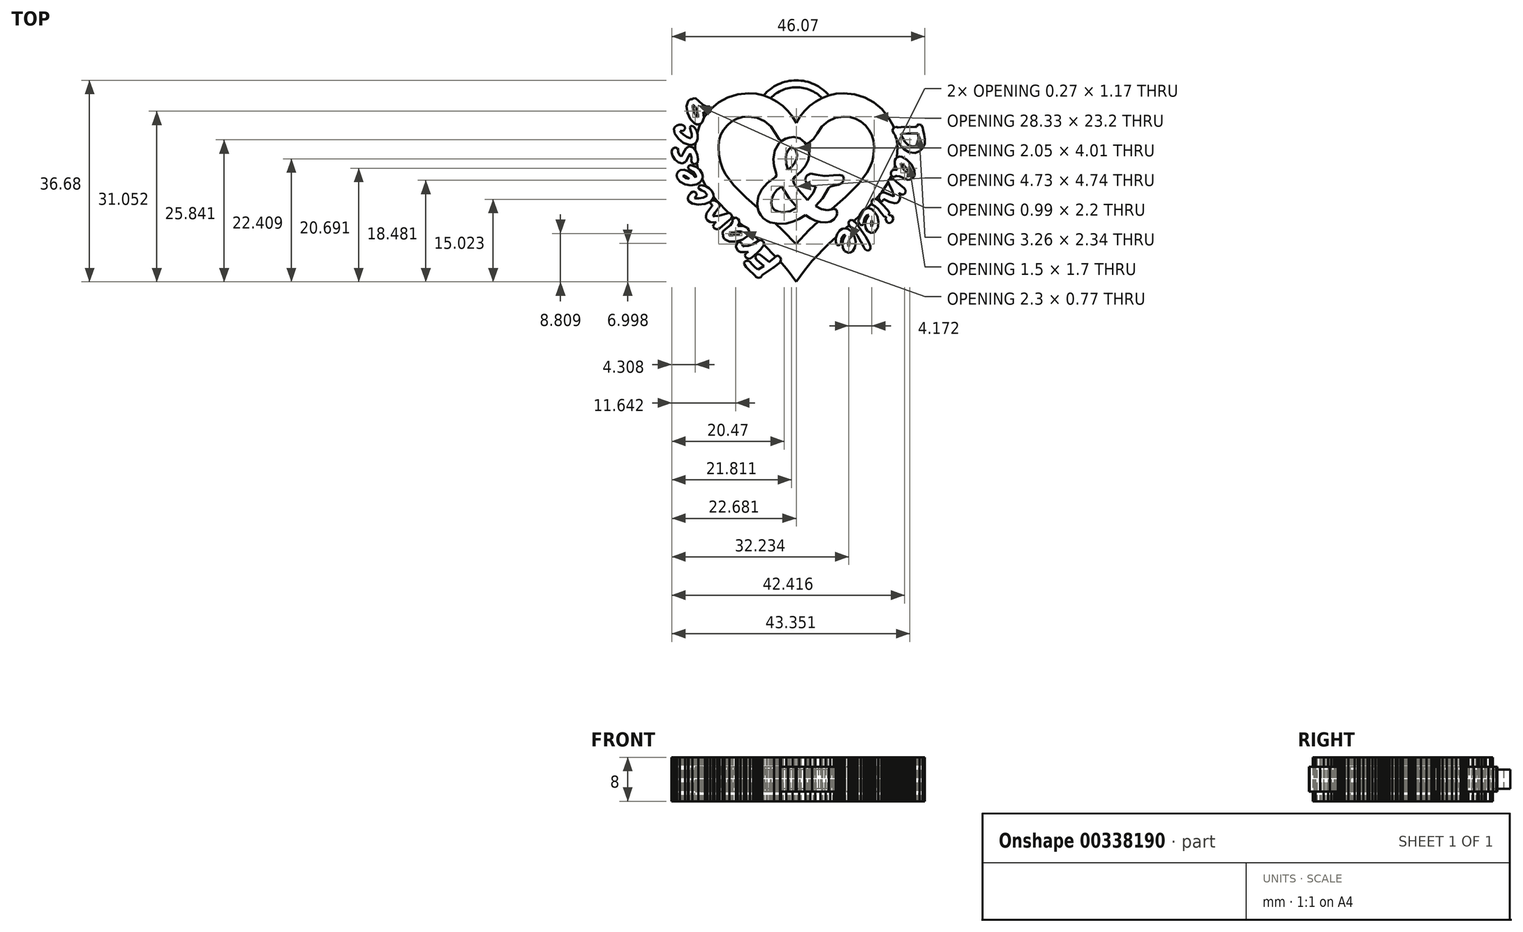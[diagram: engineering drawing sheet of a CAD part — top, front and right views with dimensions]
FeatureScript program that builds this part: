
annotation { "Feature Type Name" : "Feature", "Feature Type Description" : "" }
export const myFeature = defineFeature(function(context is Context, id is Id, definition is map)
    precondition{}
    {
        {
            var Q0;
            Q0=qCreatedBy(makeId("Top.planeOp"),FACE);
            var sketch = newSketch(context, id + "F0", { "sketchPlane" : qUnion([Q0])});
            skLineSegment(sketch, "E0", {"start": v(5.9, -10.24) * mm, "end": v(6.97, -10.8) * mm});
            skLineSegment(sketch, "E1", {"start": v(6.97, -10.8) * mm, "end": v(8.06, -10.99) * mm});
            skLineSegment(sketch, "E2", {"start": v(8.06, -10.99) * mm, "end": v(9.01, -10.77) * mm});
            skLineSegment(sketch, "E3", {"start": v(9.01, -10.77) * mm, "end": v(9.22, -10.74) * mm});
            skLineSegment(sketch, "E4", {"start": v(9.22, -10.74) * mm, "end": v(9.68, -10.95) * mm});
            skLineSegment(sketch, "E5", {"start": v(9.68, -10.95) * mm, "end": v(9.83, -11.55) * mm});
            skLineSegment(sketch, "E6", {"start": v(9.83, -11.55) * mm, "end": v(9.68, -12.04) * mm});
            skLineSegment(sketch, "E7", {"start": v(9.68, -12.04) * mm, "end": v(9.22, -12.62) * mm});
            skLineSegment(sketch, "E8", {"start": v(9.22, -12.62) * mm, "end": v(8.56, -13.08) * mm});
            skLineSegment(sketch, "E9", {"start": v(8.56, -13.08) * mm, "end": v(7.74, -13.23) * mm});
            skLineSegment(sketch, "E10", {"start": v(7.74, -13.23) * mm, "end": v(6.78, -13.15) * mm});
            skLineSegment(sketch, "E11", {"start": v(6.78, -13.15) * mm, "end": v(5.84, -12.9) * mm});
            skLineSegment(sketch, "E12", {"start": v(5.84, -12.9) * mm, "end": v(4.92, -12.48) * mm});
            skLineSegment(sketch, "E13", {"start": v(4.92, -12.48) * mm, "end": v(4.02, -11.89) * mm});
            skLineSegment(sketch, "E14", {"start": v(4.02, -11.89) * mm, "end": v(2.89, -12.59) * mm});
            skLineSegment(sketch, "E15", {"start": v(2.89, -12.59) * mm, "end": v(1.72, -13.09) * mm});
            skLineSegment(sketch, "E16", {"start": v(1.72, -13.09) * mm, "end": v(0.52, -13.39) * mm});
            skLineSegment(sketch, "E17", {"start": v(0.52, -13.39) * mm, "end": v(-0.72, -13.49) * mm});
            skLineSegment(sketch, "E18", {"start": v(-0.72, -13.49) * mm, "end": v(-2.35, -13.23) * mm});
            skLineSegment(sketch, "E19", {"start": v(-2.35, -13.23) * mm, "end": v(-3.03, -12.9) * mm});
            skLineSegment(sketch, "E20", {"start": v(-3.03, -12.9) * mm, "end": v(-3.63, -12.45) * mm});
            skLineSegment(sketch, "E21", {"start": v(-3.63, -12.45) * mm, "end": v(-4.11, -11.89) * mm});
            skLineSegment(sketch, "E22", {"start": v(-4.11, -11.89) * mm, "end": v(-4.46, -11.25) * mm});
            skLineSegment(sketch, "E23", {"start": v(-4.46, -11.25) * mm, "end": v(-4.67, -10.53) * mm});
            skLineSegment(sketch, "E24", {"start": v(-4.67, -10.53) * mm, "end": v(-4.74, -9.73) * mm});
            skLineSegment(sketch, "E25", {"start": v(-4.74, -9.73) * mm, "end": v(-4.53, -8.43) * mm});
            skLineSegment(sketch, "E26", {"start": v(-4.53, -8.43) * mm, "end": v(-3.91, -7.2) * mm});
            skLineSegment(sketch, "E27", {"start": v(-3.91, -7.2) * mm, "end": v(-2.89, -6.06) * mm});
            skLineSegment(sketch, "E28", {"start": v(-2.89, -6.06) * mm, "end": v(-1.45, -4.98) * mm});
            skLineSegment(sketch, "E29", {"start": v(-1.45, -4.98) * mm, "end": v(-1.22, -4.63) * mm});
            skLineSegment(sketch, "E30", {"start": v(-1.22, -4.63) * mm, "end": v(-1.31, -4.25) * mm});
            skLineSegment(sketch, "E31", {"start": v(-1.31, -4.25) * mm, "end": v(-1.68, -2.95) * mm});
            skLineSegment(sketch, "E32", {"start": v(-1.68, -2.95) * mm, "end": v(-1.8, -1.73) * mm});
            skLineSegment(sketch, "E33", {"start": v(-1.8, -1.73) * mm, "end": v(-1.54, -0.13) * mm});
            skLineSegment(sketch, "E34", {"start": v(-1.54, -0.13) * mm, "end": v(-0.77, 1.17) * mm});
            skLineSegment(sketch, "E35", {"start": v(-0.77, 1.17) * mm, "end": v(-0.21, 1.67) * mm});
            skLineSegment(sketch, "E36", {"start": v(-0.21, 1.67) * mm, "end": v(0.41, 2.02) * mm});
            skLineSegment(sketch, "E37", {"start": v(0.41, 2.02) * mm, "end": v(1.1, 2.24) * mm});
            skLineSegment(sketch, "E38", {"start": v(1.1, 2.24) * mm, "end": v(1.87, 2.31) * mm});
            skLineSegment(sketch, "E39", {"start": v(1.87, 2.31) * mm, "end": v(3.04, 2.07) * mm});
            skLineSegment(sketch, "E40", {"start": v(3.04, 2.07) * mm, "end": v(3.94, 1.35) * mm});
            skLineSegment(sketch, "E41", {"start": v(3.94, 1.35) * mm, "end": v(4.52, 0.31) * mm});
            skLineSegment(sketch, "E42", {"start": v(4.52, 0.31) * mm, "end": v(4.71, -0.86) * mm});
            skLineSegment(sketch, "E43", {"start": v(4.71, -0.86) * mm, "end": v(4.55, -1.9) * mm});
            skLineSegment(sketch, "E44", {"start": v(4.55, -1.9) * mm, "end": v(4.05, -2.94) * mm});
            skLineSegment(sketch, "E45", {"start": v(4.05, -2.94) * mm, "end": v(3.23, -3.96) * mm});
            skLineSegment(sketch, "E46", {"start": v(3.23, -3.96) * mm, "end": v(2.07, -4.98) * mm});
            skLineSegment(sketch, "E47", {"start": v(2.07, -4.98) * mm, "end": v(1.75, -5.47) * mm});
            skLineSegment(sketch, "E48", {"start": v(1.75, -5.47) * mm, "end": v(2.02, -6.2) * mm});
            skLineSegment(sketch, "E49", {"start": v(2.02, -6.2) * mm, "end": v(2.82, -7.37) * mm});
            skLineSegment(sketch, "E50", {"start": v(2.82, -7.37) * mm, "end": v(4.42, -9.15) * mm});
            skLineSegment(sketch, "E51", {"start": v(4.42, -9.15) * mm, "end": v(5.4, -7.88) * mm});
            skLineSegment(sketch, "E52", {"start": v(5.4, -7.88) * mm, "end": v(5.96, -6.65) * mm});
            skLineSegment(sketch, "E53", {"start": v(5.96, -6.65) * mm, "end": v(5.59, -6.6) * mm});
            skLineSegment(sketch, "E54", {"start": v(5.59, -6.6) * mm, "end": v(4.82, -6.47) * mm});
            skLineSegment(sketch, "E55", {"start": v(4.82, -6.47) * mm, "end": v(4.35, -6.22) * mm});
            skLineSegment(sketch, "E56", {"start": v(4.35, -6.22) * mm, "end": v(4.12, -5.83) * mm});
            skLineSegment(sketch, "E57", {"start": v(4.12, -5.83) * mm, "end": v(4.04, -5.33) * mm});
            skLineSegment(sketch, "E58", {"start": v(4.04, -5.33) * mm, "end": v(4.12, -4.97) * mm});
            skLineSegment(sketch, "E59", {"start": v(4.12, -4.97) * mm, "end": v(4.36, -4.65) * mm});
            skLineSegment(sketch, "E60", {"start": v(4.36, -4.65) * mm, "end": v(5, -4.34) * mm});
            skLineSegment(sketch, "E61", {"start": v(5, -4.34) * mm, "end": v(5.96, -4.55) * mm});
            skLineSegment(sketch, "E62", {"start": v(5.96, -4.55) * mm, "end": v(7.52, -4.77) * mm});
            skLineSegment(sketch, "E63", {"start": v(7.52, -4.77) * mm, "end": v(9.12, -4.67) * mm});
            skLineSegment(sketch, "E64", {"start": v(9.12, -4.67) * mm, "end": v(10.22, -4.57) * mm});
            skLineSegment(sketch, "E65", {"start": v(10.22, -4.57) * mm, "end": v(10.8, -4.73) * mm});
            skLineSegment(sketch, "E66", {"start": v(10.8, -4.73) * mm, "end": v(11, -5.2) * mm});
            skLineSegment(sketch, "E67", {"start": v(11, -5.2) * mm, "end": v(10.9, -5.72) * mm});
            skLineSegment(sketch, "E68", {"start": v(10.9, -5.72) * mm, "end": v(10.6, -6.11) * mm});
            skLineSegment(sketch, "E69", {"start": v(10.6, -6.11) * mm, "end": v(10.1, -6.37) * mm});
            skLineSegment(sketch, "E70", {"start": v(10.1, -6.37) * mm, "end": v(9.4, -6.5) * mm});
            skLineSegment(sketch, "E71", {"start": v(9.4, -6.5) * mm, "end": v(8.61, -6.65) * mm});
            skLineSegment(sketch, "E72", {"start": v(8.61, -6.65) * mm, "end": v(8.26, -7) * mm});
            skLineSegment(sketch, "E73", {"start": v(8.26, -7) * mm, "end": v(7.13, -8.84) * mm});
            skLineSegment(sketch, "E74", {"start": v(7.13, -8.84) * mm, "end": v(5.9, -10.24) * mm});
            skLineSegment(sketch, "E75", {"start": v(0.89, -3.63) * mm, "end": v(1.6, -2.98) * mm});
            skLineSegment(sketch, "E76", {"start": v(1.6, -2.98) * mm, "end": v(2.12, -2.3) * mm});
            skLineSegment(sketch, "E77", {"start": v(2.12, -2.3) * mm, "end": v(2.42, -1.62) * mm});
            skLineSegment(sketch, "E78", {"start": v(2.42, -1.62) * mm, "end": v(2.53, -0.92) * mm});
            skLineSegment(sketch, "E79", {"start": v(2.53, -0.92) * mm, "end": v(2.26, -0.02) * mm});
            skLineSegment(sketch, "E80", {"start": v(2.26, -0.02) * mm, "end": v(1.99, 0.27) * mm});
            skLineSegment(sketch, "E81", {"start": v(1.99, 0.27) * mm, "end": v(1.65, 0.37) * mm});
            skLineSegment(sketch, "E82", {"start": v(1.65, 0.37) * mm, "end": v(1.21, 0.23) * mm});
            skLineSegment(sketch, "E83", {"start": v(1.21, 0.23) * mm, "end": v(0.83, -0.18) * mm});
            skLineSegment(sketch, "E84", {"start": v(0.83, -0.18) * mm, "end": v(0.56, -0.78) * mm});
            skLineSegment(sketch, "E85", {"start": v(0.56, -0.78) * mm, "end": v(0.48, -1.49) * mm});
            skLineSegment(sketch, "E86", {"start": v(0.48, -1.49) * mm, "end": v(0.58, -2.59) * mm});
            skLineSegment(sketch, "E87", {"start": v(0.58, -2.59) * mm, "end": v(0.89, -3.63) * mm});
            skLineSegment(sketch, "E88", {"start": v(2.53, -10.51) * mm, "end": v(1.02, -8.73) * mm});
            skLineSegment(sketch, "E89", {"start": v(1.02, -8.73) * mm, "end": v(-0.3, -6.65) * mm});
            skLineSegment(sketch, "E90", {"start": v(-0.3, -6.65) * mm, "end": v(-1.14, -7.32) * mm});
            skLineSegment(sketch, "E91", {"start": v(-1.14, -7.32) * mm, "end": v(-1.73, -8.05) * mm});
            skLineSegment(sketch, "E92", {"start": v(-1.73, -8.05) * mm, "end": v(-2.09, -8.82) * mm});
            skLineSegment(sketch, "E93", {"start": v(-2.09, -8.82) * mm, "end": v(-2.2, -9.64) * mm});
            skLineSegment(sketch, "E94", {"start": v(-2.2, -9.64) * mm, "end": v(-2.06, -10.37) * mm});
            skLineSegment(sketch, "E95", {"start": v(-2.06, -10.37) * mm, "end": v(-1.62, -10.93) * mm});
            skLineSegment(sketch, "E96", {"start": v(-1.62, -10.93) * mm, "end": v(-0.93, -11.27) * mm});
            skLineSegment(sketch, "E97", {"start": v(-0.93, -11.27) * mm, "end": v(-0.03, -11.39) * mm});
            skLineSegment(sketch, "E98", {"start": v(-0.03, -11.39) * mm, "end": v(1.25, -11.17) * mm});
            skLineSegment(sketch, "E99", {"start": v(1.25, -11.17) * mm, "end": v(2.53, -10.51) * mm});
            skLineSegment(sketch, "E100", {"start": v(-6.3, 10.29) * mm, "end": v(-8.27, 10.09) * mm});
            skLineSegment(sketch, "E101", {"start": v(-8.27, 10.09) * mm, "end": v(-10.1, 9.52) * mm});
            skLineSegment(sketch, "E102", {"start": v(-10.1, 9.52) * mm, "end": v(-11.75, 8.62) * mm});
            skLineSegment(sketch, "E103", {"start": v(-11.75, 8.62) * mm, "end": v(-13.19, 7.43) * mm});
            skLineSegment(sketch, "E104", {"start": v(-13.19, 7.43) * mm, "end": v(-14.37, 5.98) * mm});
            skLineSegment(sketch, "E105", {"start": v(-14.37, 5.98) * mm, "end": v(-15.27, 4.32) * mm});
            skLineSegment(sketch, "E106", {"start": v(-15.27, 4.32) * mm, "end": v(-15.84, 2.5) * mm});
            skLineSegment(sketch, "E107", {"start": v(-16.04, 0.53) * mm, "end": v(-15.91, -1.43) * mm});
            skLineSegment(sketch, "E108", {"start": v(-15.91, -1.43) * mm, "end": v(-15.55, -3.22) * mm});
            skLineSegment(sketch, "E109", {"start": v(-15.55, -3.22) * mm, "end": v(-14.97, -4.87) * mm});
            skLineSegment(sketch, "E110", {"start": v(-14.97, -4.87) * mm, "end": v(-14.2, -6.4) * mm});
            skLineSegment(sketch, "E111", {"start": v(-14.2, -6.4) * mm, "end": v(-13.27, -7.83) * mm});
            skLineSegment(sketch, "E112", {"start": v(-13.27, -7.83) * mm, "end": v(-12.18, -9.2) * mm});
            skLineSegment(sketch, "E113", {"start": v(-12.18, -9.2) * mm, "end": v(-9.63, -11.78) * mm});
            skLineSegment(sketch, "E114", {"start": v(-9.63, -11.78) * mm, "end": v(-3.7, -17.11) * mm});
            skLineSegment(sketch, "E115", {"start": v(-3.7, -17.11) * mm, "end": v(-0.64, -20.22) * mm});
            skLineSegment(sketch, "E116", {"start": v(-0.64, -20.22) * mm, "end": v(0.84, -21.97) * mm});
            skLineSegment(sketch, "E117", {"start": v(0.84, -21.97) * mm, "end": v(2.26, -23.88) * mm});
            skLineSegment(sketch, "E118", {"start": v(2.26, -23.88) * mm, "end": v(2.37, -24.04) * mm});
            skLineSegment(sketch, "E119", {"start": v(2.37, -24.04) * mm, "end": v(2.48, -23.88) * mm});
            skLineSegment(sketch, "E120", {"start": v(2.48, -23.88) * mm, "end": v(3.84, -21.98) * mm});
            skLineSegment(sketch, "E121", {"start": v(3.84, -21.98) * mm, "end": v(5.27, -20.23) * mm});
            skLineSegment(sketch, "E122", {"start": v(5.27, -20.23) * mm, "end": v(8.27, -17.1) * mm});
            skLineSegment(sketch, "E123", {"start": v(8.27, -17.1) * mm, "end": v(14.23, -11.68) * mm});
            skLineSegment(sketch, "E124", {"start": v(14.23, -11.68) * mm, "end": v(16.81, -9.06) * mm});
            skLineSegment(sketch, "E125", {"start": v(16.81, -9.06) * mm, "end": v(17.93, -7.7) * mm});
            skLineSegment(sketch, "E126", {"start": v(17.93, -7.7) * mm, "end": v(18.89, -6.26) * mm});
            skLineSegment(sketch, "E127", {"start": v(18.89, -6.26) * mm, "end": v(19.68, -4.75) * mm});
            skLineSegment(sketch, "E128", {"start": v(19.68, -4.75) * mm, "end": v(20.28, -3.12) * mm});
            skLineSegment(sketch, "E129", {"start": v(20.28, -3.12) * mm, "end": v(20.65, -1.37) * mm});
            skLineSegment(sketch, "E130", {"start": v(20.65, -1.37) * mm, "end": v(20.78, 0.53) * mm});
            skLineSegment(sketch, "E131", {"start": v(20.78, 0.53) * mm, "end": v(20.58, 2.5) * mm});
            skLineSegment(sketch, "E132", {"start": v(20.58, 2.5) * mm, "end": v(20.01, 4.32) * mm});
            skLineSegment(sketch, "E133", {"start": v(20.01, 4.32) * mm, "end": v(19.12, 5.98) * mm});
            skLineSegment(sketch, "E134", {"start": v(19.12, 5.98) * mm, "end": v(17.93, 7.43) * mm});
            skLineSegment(sketch, "E135", {"start": v(17.93, 7.43) * mm, "end": v(16.49, 8.62) * mm});
            skLineSegment(sketch, "E136", {"start": v(16.49, 8.62) * mm, "end": v(14.84, 9.52) * mm});
            skLineSegment(sketch, "E137", {"start": v(14.84, 9.52) * mm, "end": v(13, 10.09) * mm});
            skLineSegment(sketch, "E138", {"start": v(13, 10.09) * mm, "end": v(11.05, 10.29) * mm});
            skLineSegment(sketch, "E139", {"start": v(11.05, 10.29) * mm, "end": v(9.65, 10.18) * mm});
            skLineSegment(sketch, "E140", {"start": v(9.65, 10.18) * mm, "end": v(8.3, 9.89) * mm});
            skLineSegment(sketch, "E141", {"start": v(8.3, 9.89) * mm, "end": v(7.05, 9.41) * mm});
            skLineSegment(sketch, "E142", {"start": v(7.05, 9.41) * mm, "end": v(5.88, 8.77) * mm});
            skLineSegment(sketch, "E143", {"start": v(5.88, 8.77) * mm, "end": v(4.81, 7.98) * mm});
            skLineSegment(sketch, "E144", {"start": v(4.81, 7.98) * mm, "end": v(3.86, 7.05) * mm});
            skLineSegment(sketch, "E145", {"start": v(3.86, 7.05) * mm, "end": v(3.05, 6) * mm});
            skLineSegment(sketch, "E146", {"start": v(3.05, 6) * mm, "end": v(2.37, 4.85) * mm});
            skLineSegment(sketch, "E147", {"start": v(2.37, 4.85) * mm, "end": v(1.7, 6) * mm});
            skLineSegment(sketch, "E148", {"start": v(1.7, 6) * mm, "end": v(0.88, 7.05) * mm});
            skLineSegment(sketch, "E149", {"start": v(0.88, 7.05) * mm, "end": v(-0.07, 7.98) * mm});
            skLineSegment(sketch, "E150", {"start": v(-0.07, 7.98) * mm, "end": v(-1.14, 8.77) * mm});
            skLineSegment(sketch, "E151", {"start": v(-1.14, 8.77) * mm, "end": v(-2.3, 9.41) * mm});
            skLineSegment(sketch, "E152", {"start": v(-2.3, 9.41) * mm, "end": v(-3.57, 9.89) * mm});
            skLineSegment(sketch, "E153", {"start": v(-3.57, 9.89) * mm, "end": v(-4.9, 10.18) * mm});
            skLineSegment(sketch, "E154", {"start": v(-4.9, 10.18) * mm, "end": v(-6.3, 10.29) * mm});
            skLineSegment(sketch, "E155", {"start": v(-6.3, 6.04) * mm, "end": v(-7.42, 5.93) * mm});
            skLineSegment(sketch, "E156", {"start": v(-7.42, 5.93) * mm, "end": v(-8.46, 5.61) * mm});
            skLineSegment(sketch, "E157", {"start": v(-8.46, 5.61) * mm, "end": v(-9.39, 5.11) * mm});
            skLineSegment(sketch, "E158", {"start": v(-9.39, 5.11) * mm, "end": v(-10.2, 4.44) * mm});
            skLineSegment(sketch, "E159", {"start": v(-10.2, 4.44) * mm, "end": v(-10.86, 3.63) * mm});
            skLineSegment(sketch, "E160", {"start": v(-10.86, 3.63) * mm, "end": v(-11.37, 2.7) * mm});
            skLineSegment(sketch, "E161", {"start": v(-11.37, 2.7) * mm, "end": v(-11.68, 1.65) * mm});
            skLineSegment(sketch, "E162", {"start": v(-11.68, 1.65) * mm, "end": v(-11.8, 0.53) * mm});
            skLineSegment(sketch, "E163", {"start": v(-11.8, 0.53) * mm, "end": v(-11.71, -0.9) * mm});
            skLineSegment(sketch, "E164", {"start": v(-11.71, -0.9) * mm, "end": v(-11.48, -2.17) * mm});
            skLineSegment(sketch, "E165", {"start": v(-11.48, -2.17) * mm, "end": v(-11.09, -3.32) * mm});
            skLineSegment(sketch, "E166", {"start": v(-11.09, -3.32) * mm, "end": v(-10.53, -4.4) * mm});
            skLineSegment(sketch, "E167", {"start": v(-10.53, -4.4) * mm, "end": v(-8.96, -6.48) * mm});
            skLineSegment(sketch, "E168", {"start": v(-8.96, -6.48) * mm, "end": v(-6.74, -8.68) * mm});
            skLineSegment(sketch, "E169", {"start": v(-6.74, -8.68) * mm, "end": v(-2.5, -12.45) * mm});
            skLineSegment(sketch, "E170", {"start": v(-2.5, -12.45) * mm, "end": v(-0.12, -14.65) * mm});
            skLineSegment(sketch, "E171", {"start": v(-0.12, -14.65) * mm, "end": v(2.31, -17.16) * mm});
            skLineSegment(sketch, "E172", {"start": v(2.31, -17.16) * mm, "end": v(4.7, -14.64) * mm});
            skLineSegment(sketch, "E173", {"start": v(4.7, -14.64) * mm, "end": v(7.06, -12.4) * mm});
            skLineSegment(sketch, "E174", {"start": v(7.06, -12.4) * mm, "end": v(11.33, -8.58) * mm});
            skLineSegment(sketch, "E175", {"start": v(11.33, -8.58) * mm, "end": v(13.6, -6.32) * mm});
            skLineSegment(sketch, "E176", {"start": v(13.6, -6.32) * mm, "end": v(15.23, -4.22) * mm});
            skLineSegment(sketch, "E177", {"start": v(15.23, -4.22) * mm, "end": v(15.8, -3.15) * mm});
            skLineSegment(sketch, "E178", {"start": v(15.8, -3.15) * mm, "end": v(16.2, -2.03) * mm});
            skLineSegment(sketch, "E179", {"start": v(16.2, -2.03) * mm, "end": v(16.45, -0.81) * mm});
            skLineSegment(sketch, "E180", {"start": v(16.45, -0.81) * mm, "end": v(16.53, 0.53) * mm});
            skLineSegment(sketch, "E181", {"start": v(16.53, 0.53) * mm, "end": v(16.42, 1.65) * mm});
            skLineSegment(sketch, "E182", {"start": v(16.42, 1.65) * mm, "end": v(16.1, 2.7) * mm});
            skLineSegment(sketch, "E183", {"start": v(16.1, 2.7) * mm, "end": v(15.6, 3.63) * mm});
            skLineSegment(sketch, "E184", {"start": v(15.6, 3.63) * mm, "end": v(14.94, 4.44) * mm});
            skLineSegment(sketch, "E185", {"start": v(14.94, 4.44) * mm, "end": v(14.13, 5.11) * mm});
            skLineSegment(sketch, "E186", {"start": v(14.13, 5.11) * mm, "end": v(13.2, 5.61) * mm});
            skLineSegment(sketch, "E187", {"start": v(13.2, 5.61) * mm, "end": v(12.17, 5.93) * mm});
            skLineSegment(sketch, "E188", {"start": v(12.17, 5.93) * mm, "end": v(11.05, 6.04) * mm});
            skLineSegment(sketch, "E189", {"start": v(11.05, 6.04) * mm, "end": v(9.5, 5.82) * mm});
            skLineSegment(sketch, "E190", {"start": v(9.5, 5.82) * mm, "end": v(8.14, 5.2) * mm});
            skLineSegment(sketch, "E191", {"start": v(8.14, 5.2) * mm, "end": v(7.02, 4.22) * mm});
            skLineSegment(sketch, "E192", {"start": v(7.02, 4.22) * mm, "end": v(6.17, 2.96) * mm});
            skLineSegment(sketch, "E193", {"start": v(6.17, 2.96) * mm, "end": v(5.5, 1.98) * mm});
            skLineSegment(sketch, "E194", {"start": v(5.5, 1.98) * mm, "end": v(4.6, 1.24) * mm});
            skLineSegment(sketch, "E195", {"start": v(4.6, 1.24) * mm, "end": v(3.54, 0.77) * mm});
            skLineSegment(sketch, "E196", {"start": v(3.54, 0.77) * mm, "end": v(2.37, 0.6) * mm});
            skLineSegment(sketch, "E197", {"start": v(2.37, 0.6) * mm, "end": v(1.2, 0.77) * mm});
            skLineSegment(sketch, "E198", {"start": v(1.2, 0.77) * mm, "end": v(0.14, 1.24) * mm});
            skLineSegment(sketch, "E199", {"start": v(0.14, 1.24) * mm, "end": v(-0.76, 1.98) * mm});
            skLineSegment(sketch, "E200", {"start": v(-0.76, 1.98) * mm, "end": v(-1.43, 2.96) * mm});
            skLineSegment(sketch, "E201", {"start": v(-1.43, 2.96) * mm, "end": v(-2.27, 4.22) * mm});
            skLineSegment(sketch, "E202", {"start": v(-2.27, 4.22) * mm, "end": v(-3.4, 5.2) * mm});
            skLineSegment(sketch, "E203", {"start": v(-3.4, 5.2) * mm, "end": v(-4.76, 5.82) * mm});
            skLineSegment(sketch, "E204", {"start": v(-4.76, 5.82) * mm, "end": v(-6.3, 6.04) * mm});
            skLineSegment(sketch, "E205", {"start": v(-1.06, -21.53) * mm, "end": v(-1.06, -21.54) * mm});
            skLineSegment(sketch, "E206", {"start": v(-1.06, -21.54) * mm, "end": v(-1.06, -21.54) * mm});
            skLineSegment(sketch, "E207", {"start": v(-1.06, -21.54) * mm, "end": v(-1.06, -21.53) * mm});
            skLineSegment(sketch, "E208", {"start": v(-16.09, 9.4) * mm, "end": v(-16.4, 9.34) * mm});
            skLineSegment(sketch, "E209", {"start": v(-16.4, 9.34) * mm, "end": v(-16.55, 9.2) * mm});
            skLineSegment(sketch, "E210", {"start": v(-16.55, 9.2) * mm, "end": v(-16.93, 9.2) * mm});
            skLineSegment(sketch, "E211", {"start": v(-16.93, 9.2) * mm, "end": v(-17.32, 8.89) * mm});
            skLineSegment(sketch, "E212", {"start": v(-17.32, 8.89) * mm, "end": v(-17.61, 7.94) * mm});
            skLineSegment(sketch, "E213", {"start": v(-17.61, 7.94) * mm, "end": v(-17.42, 6.73) * mm});
            skLineSegment(sketch, "E214", {"start": v(-17.42, 6.73) * mm, "end": v(-16.9, 5.6) * mm});
            skLineSegment(sketch, "E215", {"start": v(-16.9, 5.6) * mm, "end": v(-16.17, 4.82) * mm});
            skLineSegment(sketch, "E216", {"start": v(-16.17, 4.82) * mm, "end": v(-15.79, 4.64) * mm});
            skLineSegment(sketch, "E217", {"start": v(-15.79, 4.64) * mm, "end": v(-15.38, 4.62) * mm});
            skLineSegment(sketch, "E218", {"start": v(-15.38, 4.62) * mm, "end": v(-15, 4.75) * mm});
            skLineSegment(sketch, "E219", {"start": v(-15, 4.75) * mm, "end": v(-14.73, 5) * mm});
            skLineSegment(sketch, "E220", {"start": v(-14.73, 5) * mm, "end": v(-14.47, 5.81) * mm});
            skLineSegment(sketch, "E221", {"start": v(-14.47, 5.81) * mm, "end": v(-14.57, 6.84) * mm});
            skLineSegment(sketch, "E222", {"start": v(-14.57, 6.84) * mm, "end": v(-14.04, 6.63) * mm});
            skLineSegment(sketch, "E223", {"start": v(-14.04, 6.63) * mm, "end": v(-13.62, 6.67) * mm});
            skLineSegment(sketch, "E224", {"start": v(-13.62, 6.67) * mm, "end": v(-13.3, 6.92) * mm});
            skLineSegment(sketch, "E225", {"start": v(-13.3, 6.92) * mm, "end": v(-13.15, 7.4) * mm});
            skLineSegment(sketch, "E226", {"start": v(-13.15, 7.4) * mm, "end": v(-13.15, 7.4) * mm});
            skLineSegment(sketch, "E227", {"start": v(-13.15, 7.4) * mm, "end": v(-13.38, 7.9) * mm});
            skLineSegment(sketch, "E228", {"start": v(-13.38, 7.9) * mm, "end": v(-13.82, 7.89) * mm});
            skLineSegment(sketch, "E229", {"start": v(-13.82, 7.89) * mm, "end": v(-13.82, 7.89) * mm});
            skLineSegment(sketch, "E230", {"start": v(-13.82, 7.89) * mm, "end": v(-13.89, 7.84) * mm});
            skLineSegment(sketch, "E231", {"start": v(-13.89, 7.84) * mm, "end": v(-14.1, 7.9) * mm});
            skLineSegment(sketch, "E232", {"start": v(-14.1, 7.9) * mm, "end": v(-14.61, 8.18) * mm});
            skLineSegment(sketch, "E233", {"start": v(-14.61, 8.18) * mm, "end": v(-15.46, 8.93) * mm});
            skLineSegment(sketch, "E234", {"start": v(-15.46, 8.93) * mm, "end": v(-15.46, 8.93) * mm});
            skLineSegment(sketch, "E235", {"start": v(-15.46, 8.93) * mm, "end": v(-15.89, 9.32) * mm});
            skLineSegment(sketch, "E236", {"start": v(-15.89, 9.32) * mm, "end": v(-16.09, 9.4) * mm});
            skLineSegment(sketch, "E237", {"start": v(-16.09, 9.4) * mm, "end": v(-16.09, 9.4) * mm});
            skLineSegment(sketch, "E238", {"start": v(-16.42, 8.11) * mm, "end": v(-16.27, 8.05) * mm});
            skLineSegment(sketch, "E239", {"start": v(-16.27, 8.05) * mm, "end": v(-15.92, 7.65) * mm});
            skLineSegment(sketch, "E240", {"start": v(-15.92, 7.65) * mm, "end": v(-15.63, 6.93) * mm});
            skLineSegment(sketch, "E241", {"start": v(-15.63, 6.93) * mm, "end": v(-15.5, 6.3) * mm});
            skLineSegment(sketch, "E242", {"start": v(-15.5, 6.3) * mm, "end": v(-15.54, 5.91) * mm});
            skLineSegment(sketch, "E243", {"start": v(-15.54, 5.91) * mm, "end": v(-15.6, 5.95) * mm});
            skLineSegment(sketch, "E244", {"start": v(-15.6, 5.95) * mm, "end": v(-15.97, 6.35) * mm});
            skLineSegment(sketch, "E245", {"start": v(-15.97, 6.35) * mm, "end": v(-16.31, 7.08) * mm});
            skLineSegment(sketch, "E246", {"start": v(-16.31, 7.08) * mm, "end": v(-16.31, 7.08) * mm});
            skLineSegment(sketch, "E247", {"start": v(-16.31, 7.08) * mm, "end": v(-16.5, 7.8) * mm});
            skLineSegment(sketch, "E248", {"start": v(-16.5, 7.8) * mm, "end": v(-16.46, 8.1) * mm});
            skLineSegment(sketch, "E249", {"start": v(-16.46, 8.1) * mm, "end": v(-16.43, 8.1) * mm});
            skLineSegment(sketch, "E250", {"start": v(-16.43, 8.1) * mm, "end": v(-16.42, 8.11) * mm});
            skLineSegment(sketch, "E251", {"start": v(-16.42, 8.11) * mm, "end": v(-16.42, 8.11) * mm});
            skLineSegment(sketch, "E252", {"start": v(24.67, 4.62) * mm, "end": v(24.36, 4.42) * mm});
            skLineSegment(sketch, "E253", {"start": v(24.36, 4.42) * mm, "end": v(24.28, 4.15) * mm});
            skLineSegment(sketch, "E254", {"start": v(24.28, 4.15) * mm, "end": v(23.96, 4.15) * mm});
            skLineSegment(sketch, "E255", {"start": v(23.96, 4.15) * mm, "end": v(23.96, 4.15) * mm});
            skLineSegment(sketch, "E256", {"start": v(23.96, 4.15) * mm, "end": v(21.45, 4.1) * mm});
            skLineSegment(sketch, "E257", {"start": v(21.45, 4.1) * mm, "end": v(21.45, 4.1) * mm});
            skLineSegment(sketch, "E258", {"start": v(21.45, 4.1) * mm, "end": v(20.9, 4.08) * mm});
            skLineSegment(sketch, "E259", {"start": v(20.9, 4.08) * mm, "end": v(20.7, 4.13) * mm});
            skLineSegment(sketch, "E260", {"start": v(20.7, 4.13) * mm, "end": v(20.72, 4.12) * mm});
            skLineSegment(sketch, "E261", {"start": v(20.72, 4.12) * mm, "end": v(20.42, 4.17) * mm});
            skLineSegment(sketch, "E262", {"start": v(20.42, 4.17) * mm, "end": v(20.05, 3.94) * mm});
            skLineSegment(sketch, "E263", {"start": v(20.05, 3.94) * mm, "end": v(19.87, 3.45) * mm});
            skLineSegment(sketch, "E264", {"start": v(19.87, 3.45) * mm, "end": v(20.14, 2.92) * mm});
            skLineSegment(sketch, "E265", {"start": v(20.14, 2.92) * mm, "end": v(20.14, 2.92) * mm});
            skLineSegment(sketch, "E266", {"start": v(20.14, 2.92) * mm, "end": v(20.33, 2.65) * mm});
            skLineSegment(sketch, "E267", {"start": v(20.33, 2.65) * mm, "end": v(20.51, 2.23) * mm});
            skLineSegment(sketch, "E268", {"start": v(20.51, 2.23) * mm, "end": v(20.51, 2.23) * mm});
            skLineSegment(sketch, "E269", {"start": v(20.51, 2.23) * mm, "end": v(21.1, 1.06) * mm});
            skLineSegment(sketch, "E270", {"start": v(21.1, 1.06) * mm, "end": v(21.93, 0.13) * mm});
            skLineSegment(sketch, "E271", {"start": v(21.93, 0.13) * mm, "end": v(21.93, 0.13) * mm});
            skLineSegment(sketch, "E272", {"start": v(21.93, 0.13) * mm, "end": v(22.92, -0.46) * mm});
            skLineSegment(sketch, "E273", {"start": v(22.92, -0.46) * mm, "end": v(23.96, -0.57) * mm});
            skLineSegment(sketch, "E274", {"start": v(23.96, -0.57) * mm, "end": v(24.8, -0.3) * mm});
            skLineSegment(sketch, "E275", {"start": v(24.8, -0.3) * mm, "end": v(25.4, 0.29) * mm});
            skLineSegment(sketch, "E276", {"start": v(25.4, 0.29) * mm, "end": v(25.74, 1.08) * mm});
            skLineSegment(sketch, "E277", {"start": v(25.74, 1.08) * mm, "end": v(25.76, 2) * mm});
            skLineSegment(sketch, "E278", {"start": v(25.76, 2) * mm, "end": v(25.61, 2.77) * mm});
            skLineSegment(sketch, "E279", {"start": v(25.61, 2.77) * mm, "end": v(25.61, 2.77) * mm});
            skLineSegment(sketch, "E280", {"start": v(25.61, 2.77) * mm, "end": v(25.45, 3.6) * mm});
            skLineSegment(sketch, "E281", {"start": v(25.45, 3.6) * mm, "end": v(25.4, 4.05) * mm});
            skLineSegment(sketch, "E282", {"start": v(25.4, 4.05) * mm, "end": v(25.4, 4.05) * mm});
            skLineSegment(sketch, "E283", {"start": v(25.4, 4.05) * mm, "end": v(25.14, 4.47) * mm});
            skLineSegment(sketch, "E284", {"start": v(25.14, 4.47) * mm, "end": v(24.67, 4.62) * mm});
            skLineSegment(sketch, "E285", {"start": v(24.67, 4.62) * mm, "end": v(24.67, 4.62) * mm});
            skLineSegment(sketch, "E286", {"start": v(-18.93, 4.57) * mm, "end": v(-19.35, 4.44) * mm});
            skLineSegment(sketch, "E287", {"start": v(-19.35, 4.44) * mm, "end": v(-19.7, 4.17) * mm});
            skLineSegment(sketch, "E288", {"start": v(-19.7, 4.17) * mm, "end": v(-19.9, 3.8) * mm});
            skLineSegment(sketch, "E289", {"start": v(-19.9, 3.8) * mm, "end": v(-19.76, 2.94) * mm});
            skLineSegment(sketch, "E290", {"start": v(-19.76, 2.94) * mm, "end": v(-19.09, 2.04) * mm});
            skLineSegment(sketch, "E291", {"start": v(-19.09, 2.04) * mm, "end": v(-18.17, 1.3) * mm});
            skLineSegment(sketch, "E292", {"start": v(-18.17, 1.3) * mm, "end": v(-17.23, 0.92) * mm});
            skLineSegment(sketch, "E293", {"start": v(-17.23, 0.92) * mm, "end": v(-16.65, 0.9) * mm});
            skLineSegment(sketch, "E294", {"start": v(-16.65, 0.9) * mm, "end": v(-16.16, 1.08) * mm});
            skLineSegment(sketch, "E295", {"start": v(-16.16, 1.08) * mm, "end": v(-15.8, 1.47) * mm});
            skLineSegment(sketch, "E296", {"start": v(-15.8, 1.47) * mm, "end": v(-15.6, 2.02) * mm});
            skLineSegment(sketch, "E297", {"start": v(-15.6, 2.02) * mm, "end": v(-15.58, 2.76) * mm});
            skLineSegment(sketch, "E298", {"start": v(-15.58, 2.76) * mm, "end": v(-15.8, 3.5) * mm});
            skLineSegment(sketch, "E299", {"start": v(-15.8, 3.5) * mm, "end": v(-15.8, 3.5) * mm});
            skLineSegment(sketch, "E300", {"start": v(-15.8, 3.5) * mm, "end": v(-16.13, 4.08) * mm});
            skLineSegment(sketch, "E301", {"start": v(-16.13, 4.08) * mm, "end": v(-16.52, 4.36) * mm});
            skLineSegment(sketch, "E302", {"start": v(-16.52, 4.36) * mm, "end": v(-16.82, 4.3) * mm});
            skLineSegment(sketch, "E303", {"start": v(-16.82, 4.3) * mm, "end": v(-16.98, 4.05) * mm});
            skLineSegment(sketch, "E304", {"start": v(-16.98, 4.05) * mm, "end": v(-16.85, 3.47) * mm});
            skLineSegment(sketch, "E305", {"start": v(-16.85, 3.47) * mm, "end": v(-16.86, 3.47) * mm});
            skLineSegment(sketch, "E306", {"start": v(-16.86, 3.47) * mm, "end": v(-16.68, 2.9) * mm});
            skLineSegment(sketch, "E307", {"start": v(-16.68, 2.9) * mm, "end": v(-16.68, 2.39) * mm});
            skLineSegment(sketch, "E308", {"start": v(-16.68, 2.39) * mm, "end": v(-16.8, 2.15) * mm});
            skLineSegment(sketch, "E309", {"start": v(-16.8, 2.15) * mm, "end": v(-17.02, 2.13) * mm});
            skLineSegment(sketch, "E310", {"start": v(-17.02, 2.13) * mm, "end": v(-17.57, 2.33) * mm});
            skLineSegment(sketch, "E311", {"start": v(-17.57, 2.33) * mm, "end": v(-18.2, 2.78) * mm});
            skLineSegment(sketch, "E312", {"start": v(-18.2, 2.78) * mm, "end": v(-18.66, 3.25) * mm});
            skLineSegment(sketch, "E313", {"start": v(-18.66, 3.25) * mm, "end": v(-18.73, 3.4) * mm});
            skLineSegment(sketch, "E314", {"start": v(-18.73, 3.4) * mm, "end": v(-18.6, 3.4) * mm});
            skLineSegment(sketch, "E315", {"start": v(-18.6, 3.4) * mm, "end": v(-18.12, 3.48) * mm});
            skLineSegment(sketch, "E316", {"start": v(-18.12, 3.48) * mm, "end": v(-17.85, 3.86) * mm});
            skLineSegment(sketch, "E317", {"start": v(-17.85, 3.86) * mm, "end": v(-17.95, 4.26) * mm});
            skLineSegment(sketch, "E318", {"start": v(-17.95, 4.26) * mm, "end": v(-17.95, 4.26) * mm});
            skLineSegment(sketch, "E319", {"start": v(-17.95, 4.26) * mm, "end": v(-18.18, 4.46) * mm});
            skLineSegment(sketch, "E320", {"start": v(-18.18, 4.46) * mm, "end": v(-18.5, 4.56) * mm});
            skLineSegment(sketch, "E321", {"start": v(-18.5, 4.56) * mm, "end": v(-18.93, 4.57) * mm});
            skLineSegment(sketch, "E322", {"start": v(-18.93, 4.57) * mm, "end": v(-18.93, 4.57) * mm});
            skLineSegment(sketch, "E323", {"start": v(22.67, 2.97) * mm, "end": v(24.46, 2.96) * mm});
            skLineSegment(sketch, "E324", {"start": v(24.46, 2.96) * mm, "end": v(24.67, 1.98) * mm});
            skLineSegment(sketch, "E325", {"start": v(24.67, 1.98) * mm, "end": v(24.67, 1.46) * mm});
            skLineSegment(sketch, "E326", {"start": v(24.67, 1.46) * mm, "end": v(24.51, 1.05) * mm});
            skLineSegment(sketch, "E327", {"start": v(24.51, 1.05) * mm, "end": v(24.51, 1.05) * mm});
            skLineSegment(sketch, "E328", {"start": v(24.51, 1.05) * mm, "end": v(24.23, 0.77) * mm});
            skLineSegment(sketch, "E329", {"start": v(24.23, 0.77) * mm, "end": v(23.82, 0.63) * mm});
            skLineSegment(sketch, "E330", {"start": v(23.82, 0.63) * mm, "end": v(23.23, 0.67) * mm});
            skLineSegment(sketch, "E331", {"start": v(23.23, 0.67) * mm, "end": v(22.66, 0.95) * mm});
            skLineSegment(sketch, "E332", {"start": v(22.66, 0.95) * mm, "end": v(22.15, 1.45) * mm});
            skLineSegment(sketch, "E333", {"start": v(22.15, 1.45) * mm, "end": v(21.73, 2.13) * mm});
            skLineSegment(sketch, "E334", {"start": v(21.73, 2.13) * mm, "end": v(21.73, 2.13) * mm});
            skLineSegment(sketch, "E335", {"start": v(21.73, 2.13) * mm, "end": v(21.45, 2.77) * mm});
            skLineSegment(sketch, "E336", {"start": v(21.45, 2.77) * mm, "end": v(21.41, 2.89) * mm});
            skLineSegment(sketch, "E337", {"start": v(21.41, 2.89) * mm, "end": v(21.42, 2.9) * mm});
            skLineSegment(sketch, "E338", {"start": v(21.42, 2.9) * mm, "end": v(22.67, 2.97) * mm});
            skLineSegment(sketch, "E339", {"start": v(22.67, 2.97) * mm, "end": v(22.67, 2.97) * mm});
            skLineSegment(sketch, "E340", {"start": v(-17.08, 0.6) * mm, "end": v(-17.7, 0.32) * mm});
            skLineSegment(sketch, "E341", {"start": v(-17.7, 0.32) * mm, "end": v(-18.2, -0.6) * mm});
            skLineSegment(sketch, "E342", {"start": v(-18.2, -0.6) * mm, "end": v(-18.2, -0.6) * mm});
            skLineSegment(sketch, "E343", {"start": v(-18.2, -0.6) * mm, "end": v(-18.45, -1.11) * mm});
            skLineSegment(sketch, "E344", {"start": v(-18.45, -1.11) * mm, "end": v(-18.57, -1.2) * mm});
            skLineSegment(sketch, "E345", {"start": v(-18.57, -1.2) * mm, "end": v(-18.91, -0.94) * mm});
            skLineSegment(sketch, "E346", {"start": v(-18.91, -0.94) * mm, "end": v(-19.14, -0.37) * mm});
            skLineSegment(sketch, "E347", {"start": v(-19.14, -0.37) * mm, "end": v(-19.12, -0.3) * mm});
            skLineSegment(sketch, "E348", {"start": v(-19.12, -0.3) * mm, "end": v(-19.07, -0.07) * mm});
            skLineSegment(sketch, "E349", {"start": v(-19.07, -0.07) * mm, "end": v(-19.25, 0.27) * mm});
            skLineSegment(sketch, "E350", {"start": v(-19.25, 0.27) * mm, "end": v(-19.66, 0.45) * mm});
            skLineSegment(sketch, "E351", {"start": v(-19.66, 0.45) * mm, "end": v(-20.18, 0.2) * mm});
            skLineSegment(sketch, "E352", {"start": v(-20.18, 0.2) * mm, "end": v(-20.31, -0.4) * mm});
            skLineSegment(sketch, "E353", {"start": v(-20.31, -0.4) * mm, "end": v(-20.13, -1.08) * mm});
            skLineSegment(sketch, "E354", {"start": v(-20.13, -1.08) * mm, "end": v(-19.7, -1.77) * mm});
            skLineSegment(sketch, "E355", {"start": v(-19.7, -1.77) * mm, "end": v(-19.1, -2.3) * mm});
            skLineSegment(sketch, "E356", {"start": v(-19.1, -2.3) * mm, "end": v(-18.4, -2.46) * mm});
            skLineSegment(sketch, "E357", {"start": v(-18.4, -2.46) * mm, "end": v(-17.74, -2.16) * mm});
            skLineSegment(sketch, "E358", {"start": v(-17.74, -2.16) * mm, "end": v(-17.74, -2.16) * mm});
            skLineSegment(sketch, "E359", {"start": v(-17.74, -2.16) * mm, "end": v(-17.17, -1.12) * mm});
            skLineSegment(sketch, "E360", {"start": v(-17.17, -1.12) * mm, "end": v(-17.17, -1.12) * mm});
            skLineSegment(sketch, "E361", {"start": v(-17.17, -1.12) * mm, "end": v(-16.97, -0.69) * mm});
            skLineSegment(sketch, "E362", {"start": v(-16.97, -0.69) * mm, "end": v(-16.95, -0.67) * mm});
            skLineSegment(sketch, "E363", {"start": v(-16.95, -0.67) * mm, "end": v(-16.82, -0.93) * mm});
            skLineSegment(sketch, "E364", {"start": v(-16.82, -0.93) * mm, "end": v(-16.67, -1.56) * mm});
            skLineSegment(sketch, "E365", {"start": v(-16.67, -1.56) * mm, "end": v(-16.7, -1.76) * mm});
            skLineSegment(sketch, "E366", {"start": v(-16.7, -1.76) * mm, "end": v(-16.7, -1.76) * mm});
            skLineSegment(sketch, "E367", {"start": v(-16.7, -1.76) * mm, "end": v(-16.74, -2.04) * mm});
            skLineSegment(sketch, "E368", {"start": v(-16.74, -2.04) * mm, "end": v(-16.53, -2.46) * mm});
            skLineSegment(sketch, "E369", {"start": v(-16.53, -2.46) * mm, "end": v(-16.09, -2.62) * mm});
            skLineSegment(sketch, "E370", {"start": v(-16.09, -2.62) * mm, "end": v(-15.6, -2.34) * mm});
            skLineSegment(sketch, "E371", {"start": v(-15.6, -2.34) * mm, "end": v(-15.5, -1.74) * mm});
            skLineSegment(sketch, "E372", {"start": v(-15.5, -1.74) * mm, "end": v(-15.65, -0.88) * mm});
            skLineSegment(sketch, "E373", {"start": v(-15.65, -0.88) * mm, "end": v(-15.98, -0.12) * mm});
            skLineSegment(sketch, "E374", {"start": v(-15.98, -0.12) * mm, "end": v(-15.98, -0.12) * mm});
            skLineSegment(sketch, "E375", {"start": v(-15.98, -0.12) * mm, "end": v(-16.48, 0.43) * mm});
            skLineSegment(sketch, "E376", {"start": v(-16.48, 0.43) * mm, "end": v(-17.08, 0.6) * mm});
            skLineSegment(sketch, "E377", {"start": v(-17.08, 0.6) * mm, "end": v(-17.08, 0.6) * mm});
            skLineSegment(sketch, "E378", {"start": v(21.16, -1.24) * mm, "end": v(20.78, -1.35) * mm});
            skLineSegment(sketch, "E379", {"start": v(20.78, -1.35) * mm, "end": v(20.48, -1.59) * mm});
            skLineSegment(sketch, "E380", {"start": v(20.48, -1.59) * mm, "end": v(20.3, -1.92) * mm});
            skLineSegment(sketch, "E381", {"start": v(20.3, -1.92) * mm, "end": v(20.32, -2.73) * mm});
            skLineSegment(sketch, "E382", {"start": v(20.32, -2.73) * mm, "end": v(20.73, -3.63) * mm});
            skLineSegment(sketch, "E383", {"start": v(20.73, -3.63) * mm, "end": v(20.2, -3.6) * mm});
            skLineSegment(sketch, "E384", {"start": v(20.2, -3.6) * mm, "end": v(19.82, -3.77) * mm});
            skLineSegment(sketch, "E385", {"start": v(19.82, -3.77) * mm, "end": v(19.6, -4.1) * mm});
            skLineSegment(sketch, "E386", {"start": v(19.6, -4.1) * mm, "end": v(19.62, -4.6) * mm});
            skLineSegment(sketch, "E387", {"start": v(19.62, -4.6) * mm, "end": v(19.99, -4.97) * mm});
            skLineSegment(sketch, "E388", {"start": v(19.99, -4.97) * mm, "end": v(20.4, -4.83) * mm});
            skLineSegment(sketch, "E389", {"start": v(20.4, -4.83) * mm, "end": v(20.4, -4.83) * mm});
            skLineSegment(sketch, "E390", {"start": v(20.4, -4.83) * mm, "end": v(20.44, -4.77) * mm});
            skLineSegment(sketch, "E391", {"start": v(20.44, -4.77) * mm, "end": v(20.66, -4.75) * mm});
            skLineSegment(sketch, "E392", {"start": v(20.66, -4.75) * mm, "end": v(20.66, -4.75) * mm});
            skLineSegment(sketch, "E393", {"start": v(20.66, -4.75) * mm, "end": v(21.2, -4.85) * mm});
            skLineSegment(sketch, "E394", {"start": v(21.2, -4.85) * mm, "end": v(22.2, -5.26) * mm});
            skLineSegment(sketch, "E395", {"start": v(22.2, -5.26) * mm, "end": v(22.72, -5.48) * mm});
            skLineSegment(sketch, "E396", {"start": v(22.72, -5.48) * mm, "end": v(23.13, -5.41) * mm});
            skLineSegment(sketch, "E397", {"start": v(23.13, -5.41) * mm, "end": v(23.3, -5.17) * mm});
            skLineSegment(sketch, "E398", {"start": v(23.3, -5.17) * mm, "end": v(23.63, -5.04) * mm});
            skLineSegment(sketch, "E399", {"start": v(23.63, -5.04) * mm, "end": v(23.9, -4.63) * mm});
            skLineSegment(sketch, "E400", {"start": v(23.9, -4.63) * mm, "end": v(23.86, -3.68) * mm});
            skLineSegment(sketch, "E401", {"start": v(23.86, -3.68) * mm, "end": v(23.3, -2.64) * mm});
            skLineSegment(sketch, "E402", {"start": v(23.3, -2.64) * mm, "end": v(23.3, -2.64) * mm});
            skLineSegment(sketch, "E403", {"start": v(23.3, -2.64) * mm, "end": v(22.48, -1.76) * mm});
            skLineSegment(sketch, "E404", {"start": v(22.48, -1.76) * mm, "end": v(21.57, -1.29) * mm});
            skLineSegment(sketch, "E405", {"start": v(21.57, -1.29) * mm, "end": v(21.16, -1.24) * mm});
            skLineSegment(sketch, "E406", {"start": v(21.36, -2.5) * mm, "end": v(21.4, -2.5) * mm});
            skLineSegment(sketch, "E407", {"start": v(21.4, -2.5) * mm, "end": v(21.86, -2.76) * mm});
            skLineSegment(sketch, "E408", {"start": v(21.86, -2.76) * mm, "end": v(22.4, -3.3) * mm});
            skLineSegment(sketch, "E409", {"start": v(22.4, -3.3) * mm, "end": v(22.4, -3.3) * mm});
            skLineSegment(sketch, "E410", {"start": v(22.4, -3.3) * mm, "end": v(22.79, -3.9) * mm});
            skLineSegment(sketch, "E411", {"start": v(22.79, -3.9) * mm, "end": v(22.85, -4.2) * mm});
            skLineSegment(sketch, "E412", {"start": v(22.85, -4.2) * mm, "end": v(22.83, -4.2) * mm});
            skLineSegment(sketch, "E413", {"start": v(22.83, -4.2) * mm, "end": v(22.82, -4.2) * mm});
            skLineSegment(sketch, "E414", {"start": v(22.82, -4.2) * mm, "end": v(22.67, -4.2) * mm});
            skLineSegment(sketch, "E415", {"start": v(22.67, -4.2) * mm, "end": v(22.23, -3.94) * mm});
            skLineSegment(sketch, "E416", {"start": v(22.23, -3.94) * mm, "end": v(21.74, -3.38) * mm});
            skLineSegment(sketch, "E417", {"start": v(21.74, -3.38) * mm, "end": v(21.44, -2.84) * mm});
            skLineSegment(sketch, "E418", {"start": v(21.44, -2.84) * mm, "end": v(21.36, -2.5) * mm});
            skLineSegment(sketch, "E419", {"start": v(-16.77, -2.79) * mm, "end": v(-17.03, -2.83) * mm});
            skLineSegment(sketch, "E420", {"start": v(-17.03, -2.83) * mm, "end": v(-17.28, -3.04) * mm});
            skLineSegment(sketch, "E421", {"start": v(-17.28, -3.04) * mm, "end": v(-17.3, -3.37) * mm});
            skLineSegment(sketch, "E422", {"start": v(-17.3, -3.37) * mm, "end": v(-16.96, -3.67) * mm});
            skLineSegment(sketch, "E423", {"start": v(-16.96, -3.67) * mm, "end": v(-16.25, -4.1) * mm});
            skLineSegment(sketch, "E424", {"start": v(-16.25, -4.1) * mm, "end": v(-15.88, -4.62) * mm});
            skLineSegment(sketch, "E425", {"start": v(-15.88, -4.62) * mm, "end": v(-15.88, -4.9) * mm});
            skLineSegment(sketch, "E426", {"start": v(-15.88, -4.9) * mm, "end": v(-15.98, -5.01) * mm});
            skLineSegment(sketch, "E427", {"start": v(-15.98, -5.01) * mm, "end": v(-16.57, -4.33) * mm});
            skLineSegment(sketch, "E428", {"start": v(-16.57, -4.33) * mm, "end": v(-17.27, -3.86) * mm});
            skLineSegment(sketch, "E429", {"start": v(-17.27, -3.86) * mm, "end": v(-17.27, -3.86) * mm});
            skLineSegment(sketch, "E430", {"start": v(-17.27, -3.86) * mm, "end": v(-18.03, -3.64) * mm});
            skLineSegment(sketch, "E431", {"start": v(-18.03, -3.64) * mm, "end": v(-18.73, -3.72) * mm});
            skLineSegment(sketch, "E432", {"start": v(-18.73, -3.72) * mm, "end": v(-19.07, -3.93) * mm});
            skLineSegment(sketch, "E433", {"start": v(-19.07, -3.93) * mm, "end": v(-19.3, -4.26) * mm});
            skLineSegment(sketch, "E434", {"start": v(-19.3, -4.26) * mm, "end": v(-19.4, -4.67) * mm});
            skLineSegment(sketch, "E435", {"start": v(-19.4, -4.67) * mm, "end": v(-19.32, -5.1) * mm});
            skLineSegment(sketch, "E436", {"start": v(-19.32, -5.1) * mm, "end": v(-18.79, -5.82) * mm});
            skLineSegment(sketch, "E437", {"start": v(-18.79, -5.82) * mm, "end": v(-17.86, -6.3) * mm});
            skLineSegment(sketch, "E438", {"start": v(-17.86, -6.3) * mm, "end": v(-16.78, -6.48) * mm});
            skLineSegment(sketch, "E439", {"start": v(-16.78, -6.48) * mm, "end": v(-15.75, -6.29) * mm});
            skLineSegment(sketch, "E440", {"start": v(-15.75, -6.29) * mm, "end": v(-15.17, -5.96) * mm});
            skLineSegment(sketch, "E441", {"start": v(-15.17, -5.96) * mm, "end": v(-14.8, -5.5) * mm});
            skLineSegment(sketch, "E442", {"start": v(-14.8, -5.5) * mm, "end": v(-14.79, -5.5) * mm});
            skLineSegment(sketch, "E443", {"start": v(-14.79, -5.5) * mm, "end": v(-14.65, -4.94) * mm});
            skLineSegment(sketch, "E444", {"start": v(-14.65, -4.94) * mm, "end": v(-14.77, -4.33) * mm});
            skLineSegment(sketch, "E445", {"start": v(-14.77, -4.33) * mm, "end": v(-15.18, -3.63) * mm});
            skLineSegment(sketch, "E446", {"start": v(-15.18, -3.63) * mm, "end": v(-15.82, -3.1) * mm});
            skLineSegment(sketch, "E447", {"start": v(-15.82, -3.1) * mm, "end": v(-15.83, -3.1) * mm});
            skLineSegment(sketch, "E448", {"start": v(-15.83, -3.1) * mm, "end": v(-16.77, -2.79) * mm});
            skLineSegment(sketch, "E449", {"start": v(-16.77, -2.79) * mm, "end": v(-16.77, -2.79) * mm});
            skLineSegment(sketch, "E450", {"start": v(-17.97, -4.72) * mm, "end": v(-17.6, -4.88) * mm});
            skLineSegment(sketch, "E451", {"start": v(-17.6, -4.88) * mm, "end": v(-17.59, -4.88) * mm});
            skLineSegment(sketch, "E452", {"start": v(-17.59, -4.88) * mm, "end": v(-17.11, -5.26) * mm});
            skLineSegment(sketch, "E453", {"start": v(-17.11, -5.26) * mm, "end": v(-17.71, -5.15) * mm});
            skLineSegment(sketch, "E454", {"start": v(-17.71, -5.15) * mm, "end": v(-18.25, -4.79) * mm});
            skLineSegment(sketch, "E455", {"start": v(-18.25, -4.79) * mm, "end": v(-18.25, -4.77) * mm});
            skLineSegment(sketch, "E456", {"start": v(-18.25, -4.77) * mm, "end": v(-18.25, -4.77) * mm});
            skLineSegment(sketch, "E457", {"start": v(-18.25, -4.77) * mm, "end": v(-18.2, -4.72) * mm});
            skLineSegment(sketch, "E458", {"start": v(-18.2, -4.72) * mm, "end": v(-17.97, -4.72) * mm});
            skLineSegment(sketch, "E459", {"start": v(-17.97, -4.72) * mm, "end": v(-17.97, -4.72) * mm});
            skLineSegment(sketch, "E460", {"start": v(-15.94, -5.07) * mm, "end": v(-15.94, -5.07) * mm});
            skLineSegment(sketch, "E461", {"start": v(19.55, -5.2) * mm, "end": v(19.12, -5.54) * mm});
            skLineSegment(sketch, "E462", {"start": v(19.12, -5.54) * mm, "end": v(19.06, -5.87) * mm});
            skLineSegment(sketch, "E463", {"start": v(19.06, -5.87) * mm, "end": v(19.22, -6.18) * mm});
            skLineSegment(sketch, "E464", {"start": v(19.22, -6.18) * mm, "end": v(19.2, -6.17) * mm});
            skLineSegment(sketch, "E465", {"start": v(19.2, -6.17) * mm, "end": v(19.85, -7.49) * mm});
            skLineSegment(sketch, "E466", {"start": v(19.85, -7.49) * mm, "end": v(19.85, -7.49) * mm});
            skLineSegment(sketch, "E467", {"start": v(19.85, -7.49) * mm, "end": v(20.1, -8.27) * mm});
            skLineSegment(sketch, "E468", {"start": v(20.1, -8.27) * mm, "end": v(20.13, -8.5) * mm});
            skLineSegment(sketch, "E469", {"start": v(20.13, -8.5) * mm, "end": v(20.04, -8.49) * mm});
            skLineSegment(sketch, "E470", {"start": v(20.04, -8.49) * mm, "end": v(19.49, -8.23) * mm});
            skLineSegment(sketch, "E471", {"start": v(19.49, -8.23) * mm, "end": v(19.49, -8.23) * mm});
            skLineSegment(sketch, "E472", {"start": v(19.49, -8.23) * mm, "end": v(18.42, -7.77) * mm});
            skLineSegment(sketch, "E473", {"start": v(18.42, -7.77) * mm, "end": v(18.35, -7.75) * mm});
            skLineSegment(sketch, "E474", {"start": v(18.35, -7.75) * mm, "end": v(17.9, -7.8) * mm});
            skLineSegment(sketch, "E475", {"start": v(17.9, -7.8) * mm, "end": v(17.56, -8.1) * mm});
            skLineSegment(sketch, "E476", {"start": v(17.56, -8.1) * mm, "end": v(17.36, -8.8) * mm});
            skLineSegment(sketch, "E477", {"start": v(17.36, -8.8) * mm, "end": v(17.36, -8.8) * mm});
            skLineSegment(sketch, "E478", {"start": v(17.36, -8.8) * mm, "end": v(17.62, -9.34) * mm});
            skLineSegment(sketch, "E479", {"start": v(17.62, -9.34) * mm, "end": v(17.9, -9.42) * mm});
            skLineSegment(sketch, "E480", {"start": v(17.9, -9.42) * mm, "end": v(18.14, -9.26) * mm});
            skLineSegment(sketch, "E481", {"start": v(18.14, -9.26) * mm, "end": v(18.25, -9.02) * mm});
            skLineSegment(sketch, "E482", {"start": v(18.25, -9.02) * mm, "end": v(18.26, -8.98) * mm});
            skLineSegment(sketch, "E483", {"start": v(18.26, -8.98) * mm, "end": v(18.42, -9.03) * mm});
            skLineSegment(sketch, "E484", {"start": v(18.42, -9.03) * mm, "end": v(19.25, -9.44) * mm});
            skLineSegment(sketch, "E485", {"start": v(19.25, -9.44) * mm, "end": v(19.25, -9.44) * mm});
            skLineSegment(sketch, "E486", {"start": v(19.25, -9.44) * mm, "end": v(20.28, -9.75) * mm});
            skLineSegment(sketch, "E487", {"start": v(20.28, -9.75) * mm, "end": v(20.72, -9.64) * mm});
            skLineSegment(sketch, "E488", {"start": v(20.72, -9.64) * mm, "end": v(21.05, -9.33) * mm});
            skLineSegment(sketch, "E489", {"start": v(21.05, -9.33) * mm, "end": v(21.25, -8.83) * mm});
            skLineSegment(sketch, "E490", {"start": v(21.25, -8.83) * mm, "end": v(21.22, -8.23) * mm});
            skLineSegment(sketch, "E491", {"start": v(21.22, -8.23) * mm, "end": v(21.08, -7.8) * mm});
            skLineSegment(sketch, "E492", {"start": v(21.08, -7.8) * mm, "end": v(21.22, -7.92) * mm});
            skLineSegment(sketch, "E493", {"start": v(21.22, -7.92) * mm, "end": v(21.55, -8.12) * mm});
            skLineSegment(sketch, "E494", {"start": v(21.55, -8.12) * mm, "end": v(21.86, -8.17) * mm});
            skLineSegment(sketch, "E495", {"start": v(21.86, -8.17) * mm, "end": v(22.23, -7.9) * mm});
            skLineSegment(sketch, "E496", {"start": v(22.23, -7.9) * mm, "end": v(22.28, -7.38) * mm});
            skLineSegment(sketch, "E497", {"start": v(22.28, -7.38) * mm, "end": v(22, -6.97) * mm});
            skLineSegment(sketch, "E498", {"start": v(22, -6.97) * mm, "end": v(20.64, -5.86) * mm});
            skLineSegment(sketch, "E499", {"start": v(20.64, -5.86) * mm, "end": v(20.07, -5.34) * mm});
            skLineSegment(sketch, "E500", {"start": v(20.07, -5.34) * mm, "end": v(19.55, -5.2) * mm});
            skLineSegment(sketch, "E501", {"start": v(-15.04, -6.44) * mm, "end": v(-15.26, -6.53) * mm});
            skLineSegment(sketch, "E502", {"start": v(-15.26, -6.53) * mm, "end": v(-15.44, -6.77) * mm});
            skLineSegment(sketch, "E503", {"start": v(-15.44, -6.77) * mm, "end": v(-15.36, -7.07) * mm});
            skLineSegment(sketch, "E504", {"start": v(-15.36, -7.07) * mm, "end": v(-14.87, -7.38) * mm});
            skLineSegment(sketch, "E505", {"start": v(-14.87, -7.38) * mm, "end": v(-14.34, -7.66) * mm});
            skLineSegment(sketch, "E506", {"start": v(-14.34, -7.66) * mm, "end": v(-13.98, -8.03) * mm});
            skLineSegment(sketch, "E507", {"start": v(-13.98, -8.03) * mm, "end": v(-13.89, -8.27) * mm});
            skLineSegment(sketch, "E508", {"start": v(-13.89, -8.27) * mm, "end": v(-14.03, -8.45) * mm});
            skLineSegment(sketch, "E509", {"start": v(-14.03, -8.45) * mm, "end": v(-14.56, -8.69) * mm});
            skLineSegment(sketch, "E510", {"start": v(-14.56, -8.69) * mm, "end": v(-15.32, -8.82) * mm});
            skLineSegment(sketch, "E511", {"start": v(-15.32, -8.82) * mm, "end": v(-15.99, -8.82) * mm});
            skLineSegment(sketch, "E512", {"start": v(-15.99, -8.82) * mm, "end": v(-16.13, -8.77) * mm});
            skLineSegment(sketch, "E513", {"start": v(-16.13, -8.77) * mm, "end": v(-16.04, -8.67) * mm});
            skLineSegment(sketch, "E514", {"start": v(-16.04, -8.67) * mm, "end": v(-16.04, -8.67) * mm});
            skLineSegment(sketch, "E515", {"start": v(-16.04, -8.67) * mm, "end": v(-15.76, -8.27) * mm});
            skLineSegment(sketch, "E516", {"start": v(-15.76, -8.27) * mm, "end": v(-15.85, -7.82) * mm});
            skLineSegment(sketch, "E517", {"start": v(-15.85, -7.82) * mm, "end": v(-16.2, -7.6) * mm});
            skLineSegment(sketch, "E518", {"start": v(-16.2, -7.6) * mm, "end": v(-16.5, -7.63) * mm});
            skLineSegment(sketch, "E519", {"start": v(-16.5, -7.63) * mm, "end": v(-16.8, -7.8) * mm});
            skLineSegment(sketch, "E520", {"start": v(-16.8, -7.8) * mm, "end": v(-17.3, -8.47) * mm});
            skLineSegment(sketch, "E521", {"start": v(-17.3, -8.47) * mm, "end": v(-17.3, -8.47) * mm});
            skLineSegment(sketch, "E522", {"start": v(-17.3, -8.47) * mm, "end": v(-17.38, -8.92) * mm});
            skLineSegment(sketch, "E523", {"start": v(-17.38, -8.92) * mm, "end": v(-17.24, -9.31) * mm});
            skLineSegment(sketch, "E524", {"start": v(-17.24, -9.31) * mm, "end": v(-16.54, -9.82) * mm});
            skLineSegment(sketch, "E525", {"start": v(-16.54, -9.82) * mm, "end": v(-15.42, -9.98) * mm});
            skLineSegment(sketch, "E526", {"start": v(-15.42, -9.98) * mm, "end": v(-14.24, -9.85) * mm});
            skLineSegment(sketch, "E527", {"start": v(-14.24, -9.85) * mm, "end": v(-13.32, -9.45) * mm});
            skLineSegment(sketch, "E528", {"start": v(-13.32, -9.45) * mm, "end": v(-12.9, -9.05) * mm});
            skLineSegment(sketch, "E529", {"start": v(-12.9, -9.05) * mm, "end": v(-12.68, -8.57) * mm});
            skLineSegment(sketch, "E530", {"start": v(-12.68, -8.57) * mm, "end": v(-12.68, -8.57) * mm});
            skLineSegment(sketch, "E531", {"start": v(-12.68, -8.57) * mm, "end": v(-12.7, -8.04) * mm});
            skLineSegment(sketch, "E532", {"start": v(-12.7, -8.04) * mm, "end": v(-12.96, -7.51) * mm});
            skLineSegment(sketch, "E533", {"start": v(-12.96, -7.51) * mm, "end": v(-13.47, -6.98) * mm});
            skLineSegment(sketch, "E534", {"start": v(-13.47, -6.98) * mm, "end": v(-14.15, -6.61) * mm});
            skLineSegment(sketch, "E535", {"start": v(-14.15, -6.61) * mm, "end": v(-14.15, -6.61) * mm});
            skLineSegment(sketch, "E536", {"start": v(-14.15, -6.61) * mm, "end": v(-15.04, -6.44) * mm});
            skLineSegment(sketch, "E537", {"start": v(-15.04, -6.44) * mm, "end": v(-15.04, -6.44) * mm});
            skLineSegment(sketch, "E538", {"start": v(16.7, -8.88) * mm, "end": v(16.18, -9.11) * mm});
            skLineSegment(sketch, "E539", {"start": v(16.18, -9.11) * mm, "end": v(16.04, -9.57) * mm});
            skLineSegment(sketch, "E540", {"start": v(16.04, -9.57) * mm, "end": v(16.04, -9.57) * mm});
            skLineSegment(sketch, "E541", {"start": v(16.04, -9.57) * mm, "end": v(16.19, -9.96) * mm});
            skLineSegment(sketch, "E542", {"start": v(16.19, -9.96) * mm, "end": v(16.3, -10.04) * mm});
            skLineSegment(sketch, "E543", {"start": v(16.3, -10.04) * mm, "end": v(16.3, -10.04) * mm});
            skLineSegment(sketch, "E544", {"start": v(16.3, -10.04) * mm, "end": v(16.75, -10.31) * mm});
            skLineSegment(sketch, "E545", {"start": v(16.75, -10.31) * mm, "end": v(17.23, -10.75) * mm});
            skLineSegment(sketch, "E546", {"start": v(17.23, -10.75) * mm, "end": v(17.9, -11.56) * mm});
            skLineSegment(sketch, "E547", {"start": v(17.9, -11.56) * mm, "end": v(17.9, -11.57) * mm});
            skLineSegment(sketch, "E548", {"start": v(17.9, -11.57) * mm, "end": v(17.94, -11.63) * mm});
            skLineSegment(sketch, "E549", {"start": v(17.94, -11.63) * mm, "end": v(17.94, -11.63) * mm});
            skLineSegment(sketch, "E550", {"start": v(17.94, -11.63) * mm, "end": v(18.34, -12.12) * mm});
            skLineSegment(sketch, "E551", {"start": v(18.34, -12.12) * mm, "end": v(18.77, -12.2) * mm});
            skLineSegment(sketch, "E552", {"start": v(18.77, -12.2) * mm, "end": v(19.2, -11.93) * mm});
            skLineSegment(sketch, "E553", {"start": v(19.2, -11.93) * mm, "end": v(19.3, -11.4) * mm});
            skLineSegment(sketch, "E554", {"start": v(19.3, -11.4) * mm, "end": v(19.29, -11.4) * mm});
            skLineSegment(sketch, "E555", {"start": v(19.29, -11.4) * mm, "end": v(18.97, -10.96) * mm});
            skLineSegment(sketch, "E556", {"start": v(18.97, -10.96) * mm, "end": v(18.83, -10.82) * mm});
            skLineSegment(sketch, "E557", {"start": v(18.83, -10.82) * mm, "end": v(18.52, -10.46) * mm});
            skLineSegment(sketch, "E558", {"start": v(18.52, -10.46) * mm, "end": v(18.51, -10.45) * mm});
            skLineSegment(sketch, "E559", {"start": v(18.51, -10.45) * mm, "end": v(18.28, -10.2) * mm});
            skLineSegment(sketch, "E560", {"start": v(18.28, -10.2) * mm, "end": v(17.27, -9.16) * mm});
            skLineSegment(sketch, "E561", {"start": v(17.27, -9.16) * mm, "end": v(16.7, -8.88) * mm});
            skLineSegment(sketch, "E562", {"start": v(16.7, -8.88) * mm, "end": v(16.7, -8.88) * mm});
            skLineSegment(sketch, "E563", {"start": v(-12.55, -9.19) * mm, "end": v(-12.88, -9.2) * mm});
            skLineSegment(sketch, "E564", {"start": v(-12.88, -9.2) * mm, "end": v(-13.14, -9.34) * mm});
            skLineSegment(sketch, "E565", {"start": v(-13.14, -9.34) * mm, "end": v(-13.27, -9.6) * mm});
            skLineSegment(sketch, "E566", {"start": v(-13.27, -9.6) * mm, "end": v(-13.16, -9.88) * mm});
            skLineSegment(sketch, "E567", {"start": v(-13.16, -9.88) * mm, "end": v(-12.94, -10.03) * mm});
            skLineSegment(sketch, "E568", {"start": v(-12.94, -10.03) * mm, "end": v(-12.9, -10.06) * mm});
            skLineSegment(sketch, "E569", {"start": v(-12.9, -10.06) * mm, "end": v(-12.98, -10.22) * mm});
            skLineSegment(sketch, "E570", {"start": v(-12.98, -10.22) * mm, "end": v(-13.56, -11) * mm});
            skLineSegment(sketch, "E571", {"start": v(-13.56, -11) * mm, "end": v(-13.56, -11) * mm});
            skLineSegment(sketch, "E572", {"start": v(-13.56, -11) * mm, "end": v(-13.9, -11.5) * mm});
            skLineSegment(sketch, "E573", {"start": v(-13.9, -11.5) * mm, "end": v(-14.07, -11.98) * mm});
            skLineSegment(sketch, "E574", {"start": v(-14.07, -11.98) * mm, "end": v(-14.04, -12.44) * mm});
            skLineSegment(sketch, "E575", {"start": v(-14.04, -12.44) * mm, "end": v(-13.8, -12.84) * mm});
            skLineSegment(sketch, "E576", {"start": v(-13.8, -12.84) * mm, "end": v(-13.32, -13.14) * mm});
            skLineSegment(sketch, "E577", {"start": v(-13.32, -13.14) * mm, "end": v(-12.7, -13.23) * mm});
            skLineSegment(sketch, "E578", {"start": v(-12.7, -13.23) * mm, "end": v(-12.22, -13.16) * mm});
            skLineSegment(sketch, "E579", {"start": v(-12.22, -13.16) * mm, "end": v(-12.39, -13.3) * mm});
            skLineSegment(sketch, "E580", {"start": v(-12.39, -13.3) * mm, "end": v(-12.65, -13.6) * mm});
            skLineSegment(sketch, "E581", {"start": v(-12.65, -13.6) * mm, "end": v(-12.76, -13.9) * mm});
            skLineSegment(sketch, "E582", {"start": v(-12.76, -13.9) * mm, "end": v(-12.55, -14.32) * mm});
            skLineSegment(sketch, "E583", {"start": v(-12.55, -14.32) * mm, "end": v(-12.04, -14.47) * mm});
            skLineSegment(sketch, "E584", {"start": v(-12.04, -14.47) * mm, "end": v(-11.57, -14.27) * mm});
            skLineSegment(sketch, "E585", {"start": v(-11.57, -14.27) * mm, "end": v(-10.17, -13.09) * mm});
            skLineSegment(sketch, "E586", {"start": v(-10.17, -13.09) * mm, "end": v(-9.53, -12.61) * mm});
            skLineSegment(sketch, "E587", {"start": v(-9.53, -12.61) * mm, "end": v(-9.3, -12.11) * mm});
            skLineSegment(sketch, "E588", {"start": v(-9.3, -12.11) * mm, "end": v(-9.55, -11.6) * mm});
            skLineSegment(sketch, "E589", {"start": v(-9.55, -11.6) * mm, "end": v(-9.88, -11.5) * mm});
            skLineSegment(sketch, "E590", {"start": v(-9.88, -11.5) * mm, "end": v(-10.22, -11.59) * mm});
            skLineSegment(sketch, "E591", {"start": v(-10.22, -11.59) * mm, "end": v(-10.2, -11.58) * mm});
            skLineSegment(sketch, "E592", {"start": v(-10.2, -11.58) * mm, "end": v(-11.68, -11.98) * mm});
            skLineSegment(sketch, "E593", {"start": v(-11.68, -11.98) * mm, "end": v(-11.68, -11.98) * mm});
            skLineSegment(sketch, "E594", {"start": v(-11.68, -11.98) * mm, "end": v(-12.53, -12.1) * mm});
            skLineSegment(sketch, "E595", {"start": v(-12.53, -12.1) * mm, "end": v(-12.78, -12.07) * mm});
            skLineSegment(sketch, "E596", {"start": v(-12.78, -12.07) * mm, "end": v(-12.75, -11.98) * mm});
            skLineSegment(sketch, "E597", {"start": v(-12.75, -11.98) * mm, "end": v(-12.38, -11.46) * mm});
            skLineSegment(sketch, "E598", {"start": v(-12.38, -11.46) * mm, "end": v(-12.38, -11.46) * mm});
            skLineSegment(sketch, "E599", {"start": v(-12.38, -11.46) * mm, "end": v(-11.7, -10.46) * mm});
            skLineSegment(sketch, "E600", {"start": v(-11.7, -10.46) * mm, "end": v(-11.67, -10.4) * mm});
            skLineSegment(sketch, "E601", {"start": v(-11.67, -10.4) * mm, "end": v(-11.64, -9.93) * mm});
            skLineSegment(sketch, "E602", {"start": v(-11.64, -9.93) * mm, "end": v(-11.87, -9.52) * mm});
            skLineSegment(sketch, "E603", {"start": v(-11.87, -9.52) * mm, "end": v(-12.55, -9.19) * mm});
            skLineSegment(sketch, "E604", {"start": v(-12.55, -9.19) * mm, "end": v(-12.55, -9.19) * mm});
            skLineSegment(sketch, "E605", {"start": v(15.53, -10.63) * mm, "end": v(14.97, -10.71) * mm});
            skLineSegment(sketch, "E606", {"start": v(14.97, -10.71) * mm, "end": v(14.47, -11.03) * mm});
            skLineSegment(sketch, "E607", {"start": v(14.47, -11.03) * mm, "end": v(13.99, -11.65) * mm});
            skLineSegment(sketch, "E608", {"start": v(13.99, -11.65) * mm, "end": v(13.75, -12.4) * mm});
            skLineSegment(sketch, "E609", {"start": v(13.75, -12.4) * mm, "end": v(13.74, -12.4) * mm});
            skLineSegment(sketch, "E610", {"start": v(13.74, -12.4) * mm, "end": v(13.72, -13.1) * mm});
            skLineSegment(sketch, "E611", {"start": v(13.72, -13.1) * mm, "end": v(13.93, -13.6) * mm});
            skLineSegment(sketch, "E612", {"start": v(13.93, -13.6) * mm, "end": v(14.2, -13.75) * mm});
            skLineSegment(sketch, "E613", {"start": v(14.2, -13.75) * mm, "end": v(14.5, -13.64) * mm});
            skLineSegment(sketch, "E614", {"start": v(14.5, -13.64) * mm, "end": v(14.66, -13.23) * mm});
            skLineSegment(sketch, "E615", {"start": v(14.66, -13.23) * mm, "end": v(14.66, -13.23) * mm});
            skLineSegment(sketch, "E616", {"start": v(14.66, -13.23) * mm, "end": v(14.8, -12.45) * mm});
            skLineSegment(sketch, "E617", {"start": v(14.8, -12.45) * mm, "end": v(15.13, -11.94) * mm});
            skLineSegment(sketch, "E618", {"start": v(15.13, -11.94) * mm, "end": v(15.37, -11.83) * mm});
            skLineSegment(sketch, "E619", {"start": v(15.37, -11.83) * mm, "end": v(15.5, -11.89) * mm});
            skLineSegment(sketch, "E620", {"start": v(15.5, -11.89) * mm, "end": v(15.1, -12.65) * mm});
            skLineSegment(sketch, "E621", {"start": v(15.1, -12.65) * mm, "end": v(14.93, -13.44) * mm});
            skLineSegment(sketch, "E622", {"start": v(14.93, -13.44) * mm, "end": v(14.93, -13.44) * mm});
            skLineSegment(sketch, "E623", {"start": v(14.93, -13.44) * mm, "end": v(15, -14.2) * mm});
            skLineSegment(sketch, "E624", {"start": v(15, -14.2) * mm, "end": v(15.32, -14.8) * mm});
            skLineSegment(sketch, "E625", {"start": v(15.32, -14.8) * mm, "end": v(16, -15.13) * mm});
            skLineSegment(sketch, "E626", {"start": v(16, -15.13) * mm, "end": v(16.4, -15.07) * mm});
            skLineSegment(sketch, "E627", {"start": v(16.4, -15.07) * mm, "end": v(16.77, -14.85) * mm});
            skLineSegment(sketch, "E628", {"start": v(16.77, -14.85) * mm, "end": v(17.23, -14.11) * mm});
            skLineSegment(sketch, "E629", {"start": v(17.23, -14.11) * mm, "end": v(17.33, -13.1) * mm});
            skLineSegment(sketch, "E630", {"start": v(17.33, -13.1) * mm, "end": v(17.1, -12.07) * mm});
            skLineSegment(sketch, "E631", {"start": v(17.1, -12.07) * mm, "end": v(16.58, -11.22) * mm});
            skLineSegment(sketch, "E632", {"start": v(16.58, -11.22) * mm, "end": v(16.08, -10.81) * mm});
            skLineSegment(sketch, "E633", {"start": v(16.08, -10.81) * mm, "end": v(15.53, -10.63) * mm});
            skLineSegment(sketch, "E634", {"start": v(15.53, -10.63) * mm, "end": v(15.53, -10.63) * mm});
            skLineSegment(sketch, "E635", {"start": v(-8.67, -12.35) * mm, "end": v(-9.18, -12.51) * mm});
            skLineSegment(sketch, "E636", {"start": v(-9.18, -12.51) * mm, "end": v(-9.24, -12.95) * mm});
            skLineSegment(sketch, "E637", {"start": v(-9.24, -12.95) * mm, "end": v(-9.24, -12.95) * mm});
            skLineSegment(sketch, "E638", {"start": v(-9.24, -12.95) * mm, "end": v(-9.2, -13.03) * mm});
            skLineSegment(sketch, "E639", {"start": v(-9.2, -13.03) * mm, "end": v(-9.28, -13.24) * mm});
            skLineSegment(sketch, "E640", {"start": v(-9.28, -13.24) * mm, "end": v(-9.63, -13.7) * mm});
            skLineSegment(sketch, "E641", {"start": v(-9.63, -13.7) * mm, "end": v(-10.49, -14.43) * mm});
            skLineSegment(sketch, "E642", {"start": v(-10.49, -14.43) * mm, "end": v(-10.94, -14.8) * mm});
            skLineSegment(sketch, "E643", {"start": v(-10.94, -14.8) * mm, "end": v(-11.07, -15.21) * mm});
            skLineSegment(sketch, "E644", {"start": v(-11.07, -15.21) * mm, "end": v(-10.92, -15.48) * mm});
            skLineSegment(sketch, "E645", {"start": v(-10.92, -15.48) * mm, "end": v(-10.96, -15.85) * mm});
            skLineSegment(sketch, "E646", {"start": v(-10.96, -15.85) * mm, "end": v(-10.7, -16.28) * mm});
            skLineSegment(sketch, "E647", {"start": v(-10.7, -16.28) * mm, "end": v(-9.81, -16.7) * mm});
            skLineSegment(sketch, "E648", {"start": v(-9.81, -16.7) * mm, "end": v(-8.59, -16.68) * mm});
            skLineSegment(sketch, "E649", {"start": v(-8.59, -16.68) * mm, "end": v(-8.59, -16.68) * mm});
            skLineSegment(sketch, "E650", {"start": v(-8.59, -16.68) * mm, "end": v(-7.39, -16.33) * mm});
            skLineSegment(sketch, "E651", {"start": v(-7.39, -16.33) * mm, "end": v(-6.52, -15.7) * mm});
            skLineSegment(sketch, "E652", {"start": v(-6.52, -15.7) * mm, "end": v(-6.3, -15.35) * mm});
            skLineSegment(sketch, "E653", {"start": v(-6.3, -15.35) * mm, "end": v(-6.2, -14.95) * mm});
            skLineSegment(sketch, "E654", {"start": v(-6.2, -14.95) * mm, "end": v(-6.29, -14.56) * mm});
            skLineSegment(sketch, "E655", {"start": v(-6.29, -14.56) * mm, "end": v(-6.5, -14.25) * mm});
            skLineSegment(sketch, "E656", {"start": v(-6.5, -14.25) * mm, "end": v(-7.27, -13.88) * mm});
            skLineSegment(sketch, "E657", {"start": v(-7.27, -13.88) * mm, "end": v(-8.3, -13.84) * mm});
            skLineSegment(sketch, "E658", {"start": v(-8.3, -13.84) * mm, "end": v(-8.02, -13.34) * mm});
            skLineSegment(sketch, "E659", {"start": v(-8.02, -13.34) * mm, "end": v(-8, -12.92) * mm});
            skLineSegment(sketch, "E660", {"start": v(-8, -12.92) * mm, "end": v(-8.2, -12.57) * mm});
            skLineSegment(sketch, "E661", {"start": v(-8.2, -12.57) * mm, "end": v(-8.67, -12.35) * mm});
            skLineSegment(sketch, "E662", {"start": v(-8.67, -12.35) * mm, "end": v(-8.67, -12.35) * mm});
            skLineSegment(sketch, "E663", {"start": v(19.19, -11.89) * mm, "end": v(19.19, -11.89) * mm});
            skLineSegment(sketch, "E664", {"start": v(19.19, -11.89) * mm, "end": v(18.71, -12.18) * mm});
            skLineSegment(sketch, "E665", {"start": v(18.71, -12.18) * mm, "end": v(18.62, -12.72) * mm});
            skLineSegment(sketch, "E666", {"start": v(18.62, -12.72) * mm, "end": v(18.62, -12.72) * mm});
            skLineSegment(sketch, "E667", {"start": v(18.62, -12.72) * mm, "end": v(18.94, -13.28) * mm});
            skLineSegment(sketch, "E668", {"start": v(18.94, -13.28) * mm, "end": v(19.43, -13.36) * mm});
            skLineSegment(sketch, "E669", {"start": v(19.43, -13.36) * mm, "end": v(19.87, -13.05) * mm});
            skLineSegment(sketch, "E670", {"start": v(19.87, -13.05) * mm, "end": v(20.02, -12.45) * mm});
            skLineSegment(sketch, "E671", {"start": v(20.02, -12.45) * mm, "end": v(19.7, -11.98) * mm});
            skLineSegment(sketch, "E672", {"start": v(19.7, -11.98) * mm, "end": v(19.19, -11.89) * mm});
            skLineSegment(sketch, "E673", {"start": v(19.76, -12.4) * mm, "end": v(19.76, -12.4) * mm});
            skLineSegment(sketch, "E674", {"start": v(12.37, -12.75) * mm, "end": v(12.07, -12.88) * mm});
            skLineSegment(sketch, "E675", {"start": v(12.07, -12.88) * mm, "end": v(11.85, -13.34) * mm});
            skLineSegment(sketch, "E676", {"start": v(11.85, -13.34) * mm, "end": v(12.01, -13.84) * mm});
            skLineSegment(sketch, "E677", {"start": v(12.01, -13.84) * mm, "end": v(12.17, -14) * mm});
            skLineSegment(sketch, "E678", {"start": v(12.17, -14) * mm, "end": v(12.17, -14) * mm});
            skLineSegment(sketch, "E679", {"start": v(12.17, -14) * mm, "end": v(12.87, -14.72) * mm});
            skLineSegment(sketch, "E680", {"start": v(12.87, -14.72) * mm, "end": v(13.52, -15.61) * mm});
            skLineSegment(sketch, "E681", {"start": v(13.52, -15.61) * mm, "end": v(14.17, -16.76) * mm});
            skLineSegment(sketch, "E682", {"start": v(14.17, -16.76) * mm, "end": v(14.17, -16.76) * mm});
            skLineSegment(sketch, "E683", {"start": v(14.17, -16.76) * mm, "end": v(14.64, -17.74) * mm});
            skLineSegment(sketch, "E684", {"start": v(14.64, -17.74) * mm, "end": v(14.64, -17.74) * mm});
            skLineSegment(sketch, "E685", {"start": v(14.64, -17.74) * mm, "end": v(14.88, -18.11) * mm});
            skLineSegment(sketch, "E686", {"start": v(14.88, -18.11) * mm, "end": v(15.27, -18.35) * mm});
            skLineSegment(sketch, "E687", {"start": v(15.27, -18.35) * mm, "end": v(15.7, -18.2) * mm});
            skLineSegment(sketch, "E688", {"start": v(15.7, -18.2) * mm, "end": v(15.87, -17.91) * mm});
            skLineSegment(sketch, "E689", {"start": v(15.87, -17.91) * mm, "end": v(15.88, -17.54) * mm});
            skLineSegment(sketch, "E690", {"start": v(15.88, -17.54) * mm, "end": v(15.88, -17.54) * mm});
            skLineSegment(sketch, "E691", {"start": v(15.88, -17.54) * mm, "end": v(15.61, -16.88) * mm});
            skLineSegment(sketch, "E692", {"start": v(15.61, -16.88) * mm, "end": v(14.97, -15.73) * mm});
            skLineSegment(sketch, "E693", {"start": v(14.97, -15.73) * mm, "end": v(14.97, -15.73) * mm});
            skLineSegment(sketch, "E694", {"start": v(14.97, -15.73) * mm, "end": v(13.34, -13.39) * mm});
            skLineSegment(sketch, "E695", {"start": v(13.34, -13.39) * mm, "end": v(12.7, -12.8) * mm});
            skLineSegment(sketch, "E696", {"start": v(12.7, -12.8) * mm, "end": v(12.37, -12.75) * mm});
            skLineSegment(sketch, "E697", {"start": v(12.37, -12.75) * mm, "end": v(12.37, -12.75) * mm});
            skLineSegment(sketch, "E698", {"start": v(16.13, -12.82) * mm, "end": v(16.23, -13.38) * mm});
            skLineSegment(sketch, "E699", {"start": v(16.23, -13.38) * mm, "end": v(16.1, -13.99) * mm});
            skLineSegment(sketch, "E700", {"start": v(16.1, -13.99) * mm, "end": v(16.1, -13.99) * mm});
            skLineSegment(sketch, "E701", {"start": v(16.1, -13.99) * mm, "end": v(16.09, -13.99) * mm});
            skLineSegment(sketch, "E702", {"start": v(16.09, -13.99) * mm, "end": v(16.04, -13.96) * mm});
            skLineSegment(sketch, "E703", {"start": v(16.04, -13.96) * mm, "end": v(15.96, -13.37) * mm});
            skLineSegment(sketch, "E704", {"start": v(15.96, -13.37) * mm, "end": v(15.96, -13.37) * mm});
            skLineSegment(sketch, "E705", {"start": v(15.96, -13.37) * mm, "end": v(16.13, -12.82) * mm});
            skLineSegment(sketch, "E706", {"start": v(16.13, -12.82) * mm, "end": v(16.13, -12.82) * mm});
            skLineSegment(sketch, "E707", {"start": v(11.31, -14.28) * mm, "end": v(10.76, -14.37) * mm});
            skLineSegment(sketch, "E708", {"start": v(10.76, -14.37) * mm, "end": v(10.26, -14.69) * mm});
            skLineSegment(sketch, "E709", {"start": v(10.26, -14.69) * mm, "end": v(9.79, -15.32) * mm});
            skLineSegment(sketch, "E710", {"start": v(9.79, -15.32) * mm, "end": v(9.56, -16.08) * mm});
            skLineSegment(sketch, "E711", {"start": v(9.56, -16.08) * mm, "end": v(9.56, -16.08) * mm});
            skLineSegment(sketch, "E712", {"start": v(9.56, -16.08) * mm, "end": v(9.54, -16.78) * mm});
            skLineSegment(sketch, "E713", {"start": v(9.54, -16.78) * mm, "end": v(9.76, -17.26) * mm});
            skLineSegment(sketch, "E714", {"start": v(9.76, -17.26) * mm, "end": v(10.04, -17.41) * mm});
            skLineSegment(sketch, "E715", {"start": v(10.04, -17.41) * mm, "end": v(10.34, -17.3) * mm});
            skLineSegment(sketch, "E716", {"start": v(10.34, -17.3) * mm, "end": v(10.5, -16.88) * mm});
            skLineSegment(sketch, "E717", {"start": v(10.5, -16.88) * mm, "end": v(10.5, -16.88) * mm});
            skLineSegment(sketch, "E718", {"start": v(10.5, -16.88) * mm, "end": v(10.6, -16.1) * mm});
            skLineSegment(sketch, "E719", {"start": v(10.6, -16.1) * mm, "end": v(10.93, -15.59) * mm});
            skLineSegment(sketch, "E720", {"start": v(10.93, -15.59) * mm, "end": v(11.17, -15.48) * mm});
            skLineSegment(sketch, "E721", {"start": v(11.17, -15.48) * mm, "end": v(11.3, -15.53) * mm});
            skLineSegment(sketch, "E722", {"start": v(11.3, -15.53) * mm, "end": v(10.92, -16.3) * mm});
            skLineSegment(sketch, "E723", {"start": v(10.92, -16.3) * mm, "end": v(10.76, -17.1) * mm});
            skLineSegment(sketch, "E724", {"start": v(10.76, -17.1) * mm, "end": v(10.76, -17.1) * mm});
            skLineSegment(sketch, "E725", {"start": v(10.76, -17.1) * mm, "end": v(10.83, -17.85) * mm});
            skLineSegment(sketch, "E726", {"start": v(10.83, -17.85) * mm, "end": v(11.17, -18.45) * mm});
            skLineSegment(sketch, "E727", {"start": v(11.17, -18.45) * mm, "end": v(11.86, -18.77) * mm});
            skLineSegment(sketch, "E728", {"start": v(11.86, -18.77) * mm, "end": v(12.26, -18.7) * mm});
            skLineSegment(sketch, "E729", {"start": v(12.26, -18.7) * mm, "end": v(12.62, -18.47) * mm});
            skLineSegment(sketch, "E730", {"start": v(12.62, -18.47) * mm, "end": v(13.06, -17.73) * mm});
            skLineSegment(sketch, "E731", {"start": v(13.06, -17.73) * mm, "end": v(13.15, -16.73) * mm});
            skLineSegment(sketch, "E732", {"start": v(13.15, -16.73) * mm, "end": v(12.92, -15.7) * mm});
            skLineSegment(sketch, "E733", {"start": v(12.92, -15.7) * mm, "end": v(12.37, -14.85) * mm});
            skLineSegment(sketch, "E734", {"start": v(12.37, -14.85) * mm, "end": v(11.87, -14.45) * mm});
            skLineSegment(sketch, "E735", {"start": v(11.87, -14.45) * mm, "end": v(11.31, -14.28) * mm});
            skLineSegment(sketch, "E736", {"start": v(11.31, -14.28) * mm, "end": v(11.31, -14.28) * mm});
            skLineSegment(sketch, "E737", {"start": v(-7.8, -14.84) * mm, "end": v(-7.52, -14.93) * mm});
            skLineSegment(sketch, "E738", {"start": v(-7.52, -14.93) * mm, "end": v(-7.56, -14.99) * mm});
            skLineSegment(sketch, "E739", {"start": v(-7.56, -14.99) * mm, "end": v(-8.01, -15.3) * mm});
            skLineSegment(sketch, "E740", {"start": v(-8.01, -15.3) * mm, "end": v(-8.77, -15.53) * mm});
            skLineSegment(sketch, "E741", {"start": v(-8.77, -15.53) * mm, "end": v(-9.5, -15.62) * mm});
            skLineSegment(sketch, "E742", {"start": v(-9.5, -15.62) * mm, "end": v(-9.82, -15.54) * mm});
            skLineSegment(sketch, "E743", {"start": v(-9.82, -15.54) * mm, "end": v(-9.82, -15.5) * mm});
            skLineSegment(sketch, "E744", {"start": v(-9.82, -15.5) * mm, "end": v(-9.81, -15.5) * mm});
            skLineSegment(sketch, "E745", {"start": v(-9.81, -15.5) * mm, "end": v(-9.74, -15.36) * mm});
            skLineSegment(sketch, "E746", {"start": v(-9.74, -15.36) * mm, "end": v(-9.29, -15.07) * mm});
            skLineSegment(sketch, "E747", {"start": v(-9.29, -15.07) * mm, "end": v(-8.53, -14.88) * mm});
            skLineSegment(sketch, "E748", {"start": v(-8.53, -14.88) * mm, "end": v(-8.53, -14.88) * mm});
            skLineSegment(sketch, "E749", {"start": v(-8.53, -14.88) * mm, "end": v(-7.8, -14.84) * mm});
            skLineSegment(sketch, "E750", {"start": v(-7.8, -14.84) * mm, "end": v(-7.8, -14.84) * mm});
            skLineSegment(sketch, "E751", {"start": v(11.34, -15.47) * mm, "end": v(11.34, -15.47) * mm});
            skLineSegment(sketch, "E752", {"start": v(-4.13, -16.42) * mm, "end": v(-4.66, -16.66) * mm});
            skLineSegment(sketch, "E753", {"start": v(-4.66, -16.66) * mm, "end": v(-4.66, -16.66) * mm});
            skLineSegment(sketch, "E754", {"start": v(-4.66, -16.66) * mm, "end": v(-5.46, -17.18) * mm});
            skLineSegment(sketch, "E755", {"start": v(-5.46, -17.18) * mm, "end": v(-6.37, -17.47) * mm});
            skLineSegment(sketch, "E756", {"start": v(-6.37, -17.47) * mm, "end": v(-7.15, -17.56) * mm});
            skLineSegment(sketch, "E757", {"start": v(-7.15, -17.56) * mm, "end": v(-7.41, -17.52) * mm});
            skLineSegment(sketch, "E758", {"start": v(-7.41, -17.52) * mm, "end": v(-7.42, -17.44) * mm});
            skLineSegment(sketch, "E759", {"start": v(-7.42, -17.44) * mm, "end": v(-7.42, -17.44) * mm});
            skLineSegment(sketch, "E760", {"start": v(-7.42, -17.44) * mm, "end": v(-7.65, -16.9) * mm});
            skLineSegment(sketch, "E761", {"start": v(-7.65, -16.9) * mm, "end": v(-8.07, -16.8) * mm});
            skLineSegment(sketch, "E762", {"start": v(-8.07, -16.8) * mm, "end": v(-8.08, -16.8) * mm});
            skLineSegment(sketch, "E763", {"start": v(-8.08, -16.8) * mm, "end": v(-8.43, -17.02) * mm});
            skLineSegment(sketch, "E764", {"start": v(-8.43, -17.02) * mm, "end": v(-8.6, -17.32) * mm});
            skLineSegment(sketch, "E765", {"start": v(-8.6, -17.32) * mm, "end": v(-8.62, -17.67) * mm});
            skLineSegment(sketch, "E766", {"start": v(-8.62, -17.67) * mm, "end": v(-8.26, -18.34) * mm});
            skLineSegment(sketch, "E767", {"start": v(-8.26, -18.34) * mm, "end": v(-7.74, -18.6) * mm});
            skLineSegment(sketch, "E768", {"start": v(-7.74, -18.6) * mm, "end": v(-7.04, -18.64) * mm});
            skLineSegment(sketch, "E769", {"start": v(-7.04, -18.64) * mm, "end": v(-7.04, -18.64) * mm});
            skLineSegment(sketch, "E770", {"start": v(-7.04, -18.64) * mm, "end": v(-6.39, -18.53) * mm});
            skLineSegment(sketch, "E771", {"start": v(-6.39, -18.53) * mm, "end": v(-6.84, -18.86) * mm});
            skLineSegment(sketch, "E772", {"start": v(-6.84, -18.86) * mm, "end": v(-6.99, -19.24) * mm});
            skLineSegment(sketch, "E773", {"start": v(-6.99, -19.24) * mm, "end": v(-6.78, -19.66) * mm});
            skLineSegment(sketch, "E774", {"start": v(-6.78, -19.66) * mm, "end": v(-6.35, -19.85) * mm});
            skLineSegment(sketch, "E775", {"start": v(-6.35, -19.85) * mm, "end": v(-5.93, -19.77) * mm});
            skLineSegment(sketch, "E776", {"start": v(-5.93, -19.77) * mm, "end": v(-5.93, -19.77) * mm});
            skLineSegment(sketch, "E777", {"start": v(-5.93, -19.77) * mm, "end": v(-5.52, -19.45) * mm});
            skLineSegment(sketch, "E778", {"start": v(-5.52, -19.45) * mm, "end": v(-5.52, -19.45) * mm});
            skLineSegment(sketch, "E779", {"start": v(-5.52, -19.45) * mm, "end": v(-5.34, -19.29) * mm});
            skLineSegment(sketch, "E780", {"start": v(-5.34, -19.29) * mm, "end": v(-5.34, -19.29) * mm});
            skLineSegment(sketch, "E781", {"start": v(-5.34, -19.29) * mm, "end": v(-4.6, -18.59) * mm});
            skLineSegment(sketch, "E782", {"start": v(-4.6, -18.59) * mm, "end": v(-4.6, -18.59) * mm});
            skLineSegment(sketch, "E783", {"start": v(-4.6, -18.59) * mm, "end": v(-4.1, -18.08) * mm});
            skLineSegment(sketch, "E784", {"start": v(-4.1, -18.08) * mm, "end": v(-3.53, -17.29) * mm});
            skLineSegment(sketch, "E785", {"start": v(-3.53, -17.29) * mm, "end": v(-3.53, -17.29) * mm});
            skLineSegment(sketch, "E786", {"start": v(-3.53, -17.29) * mm, "end": v(-3.49, -16.93) * mm});
            skLineSegment(sketch, "E787", {"start": v(-3.49, -16.93) * mm, "end": v(-3.65, -16.63) * mm});
            skLineSegment(sketch, "E788", {"start": v(-3.65, -16.63) * mm, "end": v(-4.13, -16.42) * mm});
            skLineSegment(sketch, "E789", {"start": v(-4.13, -16.42) * mm, "end": v(-4.13, -16.42) * mm});
            skLineSegment(sketch, "E790", {"start": v(11.95, -16.46) * mm, "end": v(12.06, -17.02) * mm});
            skLineSegment(sketch, "E791", {"start": v(12.06, -17.02) * mm, "end": v(11.94, -17.62) * mm});
            skLineSegment(sketch, "E792", {"start": v(11.94, -17.62) * mm, "end": v(11.94, -17.63) * mm});
            skLineSegment(sketch, "E793", {"start": v(11.94, -17.63) * mm, "end": v(11.93, -17.62) * mm});
            skLineSegment(sketch, "E794", {"start": v(11.93, -17.62) * mm, "end": v(11.87, -17.6) * mm});
            skLineSegment(sketch, "E795", {"start": v(11.87, -17.6) * mm, "end": v(11.8, -17) * mm});
            skLineSegment(sketch, "E796", {"start": v(11.8, -17) * mm, "end": v(11.8, -17) * mm});
            skLineSegment(sketch, "E797", {"start": v(11.8, -17) * mm, "end": v(11.95, -16.46) * mm});
            skLineSegment(sketch, "E798", {"start": v(11.95, -16.46) * mm, "end": v(11.95, -16.46) * mm});
            skLineSegment(sketch, "E799", {"start": v(-4.6, -18.99) * mm, "end": v(-4.94, -19.08) * mm});
            skLineSegment(sketch, "E800", {"start": v(-4.94, -19.08) * mm, "end": v(-5.12, -19.54) * mm});
            skLineSegment(sketch, "E801", {"start": v(-5.12, -19.54) * mm, "end": v(-4.87, -20) * mm});
            skLineSegment(sketch, "E802", {"start": v(-4.87, -20) * mm, "end": v(-4.36, -20.45) * mm});
            skLineSegment(sketch, "E803", {"start": v(-4.36, -20.45) * mm, "end": v(-4.36, -20.45) * mm});
            skLineSegment(sketch, "E804", {"start": v(-4.36, -20.45) * mm, "end": v(-3.58, -21.1) * mm});
            skLineSegment(sketch, "E805", {"start": v(-3.58, -21.1) * mm, "end": v(-3.57, -21.1) * mm});
            skLineSegment(sketch, "E806", {"start": v(-3.57, -21.1) * mm, "end": v(-3.54, -21.13) * mm});
            skLineSegment(sketch, "E807", {"start": v(-3.54, -21.13) * mm, "end": v(-4.57, -21.78) * mm});
            skLineSegment(sketch, "E808", {"start": v(-4.57, -21.78) * mm, "end": v(-5.08, -21.4) * mm});
            skLineSegment(sketch, "E809", {"start": v(-5.08, -21.4) * mm, "end": v(-5.08, -21.4) * mm});
            skLineSegment(sketch, "E810", {"start": v(-5.08, -21.4) * mm, "end": v(-5.8, -20.72) * mm});
            skLineSegment(sketch, "E811", {"start": v(-5.8, -20.72) * mm, "end": v(-5.96, -20.51) * mm});
            skLineSegment(sketch, "E812", {"start": v(-5.96, -20.51) * mm, "end": v(-5.95, -20.53) * mm});
            skLineSegment(sketch, "E813", {"start": v(-5.95, -20.53) * mm, "end": v(-6.06, -20.38) * mm});
            skLineSegment(sketch, "E814", {"start": v(-6.06, -20.38) * mm, "end": v(-6.22, -20.28) * mm});
            skLineSegment(sketch, "E815", {"start": v(-6.22, -20.28) * mm, "end": v(-6.32, -20.21) * mm});
            skLineSegment(sketch, "E816", {"start": v(-6.32, -20.21) * mm, "end": v(-6.33, -20.21) * mm});
            skLineSegment(sketch, "E817", {"start": v(-6.33, -20.21) * mm, "end": v(-6.33, -20.21) * mm});
            skLineSegment(sketch, "E818", {"start": v(-6.33, -20.21) * mm, "end": v(-6.7, -20.2) * mm});
            skLineSegment(sketch, "E819", {"start": v(-6.7, -20.2) * mm, "end": v(-7.03, -20.36) * mm});
            skLineSegment(sketch, "E820", {"start": v(-7.03, -20.36) * mm, "end": v(-7.13, -20.6) * mm});
            skLineSegment(sketch, "E821", {"start": v(-7.13, -20.6) * mm, "end": v(-7.1, -20.81) * mm});
            skLineSegment(sketch, "E822", {"start": v(-7.1, -20.81) * mm, "end": v(-6.78, -21.36) * mm});
            skLineSegment(sketch, "E823", {"start": v(-6.78, -21.36) * mm, "end": v(-6.07, -22.03) * mm});
            skLineSegment(sketch, "E824", {"start": v(-6.07, -22.03) * mm, "end": v(-6.07, -22.03) * mm});
            skLineSegment(sketch, "E825", {"start": v(-6.07, -22.03) * mm, "end": v(-5.48, -22.55) * mm});
            skLineSegment(sketch, "E826", {"start": v(-5.48, -22.55) * mm, "end": v(-5.24, -22.77) * mm});
            skLineSegment(sketch, "E827", {"start": v(-5.24, -22.77) * mm, "end": v(-5.1, -22.96) * mm});
            skLineSegment(sketch, "E828", {"start": v(-5.1, -22.96) * mm, "end": v(-4.97, -23.14) * mm});
            skLineSegment(sketch, "E829", {"start": v(-4.97, -23.14) * mm, "end": v(-4.55, -23.31) * mm});
            skLineSegment(sketch, "E830", {"start": v(-4.55, -23.31) * mm, "end": v(-4.1, -23.2) * mm});
            skLineSegment(sketch, "E831", {"start": v(-4.1, -23.2) * mm, "end": v(-3.92, -22.94) * mm});
            skLineSegment(sketch, "E832", {"start": v(-3.92, -22.94) * mm, "end": v(-3.92, -22.93) * mm});
            skLineSegment(sketch, "E833", {"start": v(-3.92, -22.93) * mm, "end": v(-3.84, -22.83) * mm});
            skLineSegment(sketch, "E834", {"start": v(-3.84, -22.83) * mm, "end": v(-2.25, -21.74) * mm});
            skLineSegment(sketch, "E835", {"start": v(-2.25, -21.74) * mm, "end": v(-1.83, -21.45) * mm});
            skLineSegment(sketch, "E836", {"start": v(-1.83, -21.45) * mm, "end": v(-1.73, -21.38) * mm});
            skLineSegment(sketch, "E837", {"start": v(-1.73, -21.38) * mm, "end": v(-1.7, -21.36) * mm});
            skLineSegment(sketch, "E838", {"start": v(-1.7, -21.36) * mm, "end": v(-1.68, -21.35) * mm});
            skLineSegment(sketch, "E839", {"start": v(-1.68, -21.35) * mm, "end": v(-0.62, -20.53) * mm});
            skLineSegment(sketch, "E840", {"start": v(-0.62, -20.53) * mm, "end": v(-0.39, -19.98) * mm});
            skLineSegment(sketch, "E841", {"start": v(-0.39, -19.98) * mm, "end": v(-0.39, -19.97) * mm});
            skLineSegment(sketch, "E842", {"start": v(-0.39, -19.97) * mm, "end": v(-0.59, -19.48) * mm});
            skLineSegment(sketch, "E843", {"start": v(-0.59, -19.48) * mm, "end": v(-1, -19.27) * mm});
            skLineSegment(sketch, "E844", {"start": v(-1, -19.27) * mm, "end": v(-1.44, -19.46) * mm});
            skLineSegment(sketch, "E845", {"start": v(-1.44, -19.46) * mm, "end": v(-1.44, -19.46) * mm});
            skLineSegment(sketch, "E846", {"start": v(-1.44, -19.46) * mm, "end": v(-1.76, -19.78) * mm});
            skLineSegment(sketch, "E847", {"start": v(-1.76, -19.78) * mm, "end": v(-2.28, -20.21) * mm});
            skLineSegment(sketch, "E848", {"start": v(-2.28, -20.21) * mm, "end": v(-2.51, -20.39) * mm});
            skLineSegment(sketch, "E849", {"start": v(-2.51, -20.39) * mm, "end": v(-2.54, -20.41) * mm});
            skLineSegment(sketch, "E850", {"start": v(-2.54, -20.41) * mm, "end": v(-3.1, -19.97) * mm});
            skLineSegment(sketch, "E851", {"start": v(-3.1, -19.97) * mm, "end": v(-3.83, -19.35) * mm});
            skLineSegment(sketch, "E852", {"start": v(-3.83, -19.35) * mm, "end": v(-3.84, -19.35) * mm});
            skLineSegment(sketch, "E853", {"start": v(-3.84, -19.35) * mm, "end": v(-4.25, -19.06) * mm});
            skLineSegment(sketch, "E854", {"start": v(-4.25, -19.06) * mm, "end": v(-4.6, -18.99) * mm});
            skLineSegment(sketch, "E855", {"start": v(-4.6, -18.99) * mm, "end": v(-4.6, -18.99) * mm});
            skLineSegment(sketch, "E856", {"start": v(-15.84, 2.5) * mm, "end": v(-16.04, 0.53) * mm});
            skArc(sketch, "E857", {"start": v(-3.57, 9.89) * mm, "mid": v(2.37, 12.64) * mm, "end": v(8.3, 9.89) * mm});
            skArc(sketch, "E858", {"start": v(-2.3, 9.41) * mm, "mid": v(2.37, 11.38) * mm, "end": v(7.05, 9.41) * mm});
            skSolve(sketch);
        }
        {
            var Q0;
            Q0=makeQuery(id+"F0.imprint","IMPRINT",FACE,{"disambiguationData":[TD([[makeQuery(id+"F0.imprint","IMPRINT",EDGE,{"derivedFrom":sQuery(id+"F0.wireOp",EDGE,"E208")}),1.0]])]});
            var Q1;
            Q1=makeQuery(id+"F0.imprint","IMPRINT",FACE,{"disambiguationData":[TD([[makeQuery(id+"F0.imprint","IMPRINT",EDGE,{"derivedFrom":sQuery(id+"F0.wireOp",EDGE,"E286")}),1.0]])]});
            var Q2;
            {var subQ8=sQuery(id+"F0.wireOp",EDGE,"E224");Q2=makeQuery(id+"F0.imprint","IMPRINT",FACE,{"disambiguationData":[TD([[makeQuery(id+"F0.imprint","IMPRINT",EDGE,{"derivedFrom":subQ8}),1.0]])]});}
            var Q3;
            {var subQ6=sQuery(id+"F0.wireOp",EDGE,"E219");Q3=makeQuery(id+"F0.imprint","IMPRINT",FACE,{"disambiguationData":[TD([[makeQuery(id+"F0.imprint","IMPRINT",EDGE,{"derivedFrom":subQ6}),1.0]])]});}
            var Q4;
            {var subQ6=sQuery(id+"F0.wireOp",EDGE,"E296");Q4=makeQuery(id+"F0.imprint","IMPRINT",FACE,{"disambiguationData":[TD([[makeQuery(id+"F0.imprint","IMPRINT",EDGE,{"derivedFrom":subQ6}),1.0]])]});}
            var Q5;
            Q5=makeQuery(id+"F0.imprint","IMPRINT",FACE,{"disambiguationData":[TD([[makeQuery(id+"F0.imprint","IMPRINT",EDGE,{"derivedFrom":sQuery(id+"F0.wireOp",EDGE,"E340")}),1.0]])]});
            var Q6;
            {var subQ7=sQuery(id+"F0.wireOp",EDGE,"E371");Q6=makeQuery(id+"F0.imprint","IMPRINT",FACE,{"disambiguationData":[TD([[makeQuery(id+"F0.imprint","IMPRINT",EDGE,{"derivedFrom":subQ7}),1.0]])]});}
            var Q7;
            Q7=makeQuery(id+"F0.imprint","IMPRINT",FACE,{"disambiguationData":[TD([[makeQuery(id+"F0.imprint","IMPRINT",EDGE,{"derivedFrom":sQuery(id+"F0.wireOp",EDGE,"E419")}),1.0]])]});
            var Q8;
            {var subQ4=sQuery(id+"F0.wireOp",EDGE,"E444");Q8=makeQuery(id+"F0.imprint","IMPRINT",FACE,{"disambiguationData":[TD([[makeQuery(id+"F0.imprint","IMPRINT",EDGE,{"derivedFrom":subQ4}),1.0]])]});}
            var Q9;
            Q9=makeQuery(id+"F0.imprint","IMPRINT",FACE,{"disambiguationData":[TD([[makeQuery(id+"F0.imprint","IMPRINT",EDGE,{"derivedFrom":sQuery(id+"F0.wireOp",EDGE,"E501")}),1.0]])]});
            var Q10;
            {var subQ4=sQuery(id+"F0.wireOp",EDGE,"E532");Q10=makeQuery(id+"F0.imprint","IMPRINT",FACE,{"disambiguationData":[TD([[makeQuery(id+"F0.imprint","IMPRINT",EDGE,{"derivedFrom":subQ4}),1.0]])]});}
            var Q11;
            Q11=makeQuery(id+"F0.imprint","IMPRINT",FACE,{"disambiguationData":[TD([[makeQuery(id+"F0.imprint","IMPRINT",EDGE,{"derivedFrom":sQuery(id+"F0.wireOp",EDGE,"E563")}),1.0]])]});
            var Q12;
            {var subQ5=sQuery(id+"F0.wireOp",EDGE,"E589");Q12=makeQuery(id+"F0.imprint","IMPRINT",FACE,{"disambiguationData":[TD([[makeQuery(id+"F0.imprint","IMPRINT",EDGE,{"derivedFrom":subQ5}),1.0]])]});}
            var Q13;
            {var subQ14=sQuery(id+"F0.wireOp",EDGE,"E636");Q13=makeQuery(id+"F0.imprint","IMPRINT",FACE,{"disambiguationData":[TD([[makeQuery(id+"F0.imprint","IMPRINT",EDGE,{"derivedFrom":subQ14}),1.0]])]});}
            var Q14;
            {var subQ1=sQuery(id+"F0.wireOp",EDGE,"E660");Q14=makeQuery(id+"F0.imprint","IMPRINT",FACE,{"disambiguationData":[TD([[makeQuery(id+"F0.imprint","IMPRINT",EDGE,{"derivedFrom":subQ1}),1.0]])]});}
            var Q15;
            {var subQ0=sQuery(id+"F0.wireOp",EDGE,"E753");Q15=makeQuery(id+"F0.imprint","IMPRINT",FACE,{"disambiguationData":[TD([[makeQuery(id+"F0.imprint","IMPRINT",EDGE,{"derivedFrom":subQ0}),1.0]])]});}
            var Q16;
            {var subQ6=sQuery(id+"F0.wireOp",EDGE,"E787");Q16=makeQuery(id+"F0.imprint","IMPRINT",FACE,{"disambiguationData":[TD([[makeQuery(id+"F0.imprint","IMPRINT",EDGE,{"derivedFrom":subQ6}),1.0]])]});}
            var Q17;
            Q17=makeQuery(id+"F0.imprint","IMPRINT",FACE,{"disambiguationData":[TD([[makeQuery(id+"F0.imprint","IMPRINT",EDGE,{"derivedFrom":sQuery(id+"F0.wireOp",EDGE,"E799")}),1.0]])]});
            var Q18;
            {var subQ1=sQuery(id+"F0.wireOp",EDGE,"E841");Q18=makeQuery(id+"F0.imprint","IMPRINT",FACE,{"disambiguationData":[TD([[makeQuery(id+"F0.imprint","IMPRINT",EDGE,{"derivedFrom":subQ1}),1.0]])]});}
            var Q19;
            Q19=makeQuery(id+"F0.imprint","IMPRINT",FACE,{"disambiguationData":[TD([[makeQuery(id+"F0.imprint","IMPRINT",EDGE,{"derivedFrom":sQuery(id+"F0.wireOp",EDGE,"E707")}),1.0]])]});
            var Q20;
            {var subQ0=sQuery(id+"F0.wireOp",EDGE,"E711");Q20=makeQuery(id+"F0.imprint","IMPRINT",FACE,{"disambiguationData":[TD([[makeQuery(id+"F0.imprint","IMPRINT",EDGE,{"derivedFrom":subQ0}),1.0]])]});}
            var Q21;
            {var subQ0=sQuery(id+"F0.wireOp",EDGE,"E677");Q21=makeQuery(id+"F0.imprint","IMPRINT",FACE,{"disambiguationData":[TD([[makeQuery(id+"F0.imprint","IMPRINT",EDGE,{"derivedFrom":subQ0}),1.0]])]});}
            var Q22;
            Q22=makeQuery(id+"F0.imprint","IMPRINT",FACE,{"disambiguationData":[TD([[makeQuery(id+"F0.imprint","IMPRINT",EDGE,{"derivedFrom":sQuery(id+"F0.wireOp",EDGE,"E674")}),1.0]])]});
            var Q23;
            {var subQ0=sQuery(id+"F0.wireOp",EDGE,"E609");Q23=makeQuery(id+"F0.imprint","IMPRINT",FACE,{"disambiguationData":[TD([[makeQuery(id+"F0.imprint","IMPRINT",EDGE,{"derivedFrom":subQ0}),1.0]])]});}
            var Q24;
            {var subQ4=sQuery(id+"F0.wireOp",EDGE,"E606");Q24=makeQuery(id+"F0.imprint","IMPRINT",FACE,{"disambiguationData":[TD([[makeQuery(id+"F0.imprint","IMPRINT",EDGE,{"derivedFrom":subQ4}),1.0]])]});}
            var Q25;
            {var subQ6=sQuery(id+"F0.wireOp",EDGE,"E542");Q25=makeQuery(id+"F0.imprint","IMPRINT",FACE,{"disambiguationData":[TD([[makeQuery(id+"F0.imprint","IMPRINT",EDGE,{"derivedFrom":subQ6}),1.0]])]});}
            var Q26;
            {var subQ5=sQuery(id+"F0.wireOp",EDGE,"E538");Q26=makeQuery(id+"F0.imprint","IMPRINT",FACE,{"disambiguationData":[TD([[makeQuery(id+"F0.imprint","IMPRINT",EDGE,{"derivedFrom":subQ5}),1.0]])]});}
            var Q27;
            {var subQ7=sQuery(id+"F0.wireOp",EDGE,"E464");Q27=makeQuery(id+"F0.imprint","IMPRINT",FACE,{"disambiguationData":[TD([[makeQuery(id+"F0.imprint","IMPRINT",EDGE,{"derivedFrom":subQ7}),1.0]])]});}
            var Q28;
            {var subQ0=sQuery(id+"F0.wireOp",EDGE,"E462");Q28=makeQuery(id+"F0.imprint","IMPRINT",FACE,{"disambiguationData":[TD([[makeQuery(id+"F0.imprint","IMPRINT",EDGE,{"derivedFrom":subQ0}),1.0]])]});}
            var Q29;
            {var subQ4=sQuery(id+"F0.wireOp",EDGE,"E385");Q29=makeQuery(id+"F0.imprint","IMPRINT",FACE,{"disambiguationData":[TD([[makeQuery(id+"F0.imprint","IMPRINT",EDGE,{"derivedFrom":subQ4}),1.0]])]});}
            var Q30;
            {var subQ4=sQuery(id+"F0.wireOp",EDGE,"E380");Q30=makeQuery(id+"F0.imprint","IMPRINT",FACE,{"disambiguationData":[TD([[makeQuery(id+"F0.imprint","IMPRINT",EDGE,{"derivedFrom":subQ4}),1.0]])]});}
            var Q31;
            Q31=makeQuery(id+"F0.imprint","IMPRINT",FACE,{"disambiguationData":[TD([[makeQuery(id+"F0.imprint","IMPRINT",EDGE,{"derivedFrom":sQuery(id+"F0.wireOp",EDGE,"E252")}),1.0]])]});
            var Q32;
            {var subQ5=sQuery(id+"F0.wireOp",EDGE,"E263");Q32=makeQuery(id+"F0.imprint","IMPRINT",FACE,{"disambiguationData":[TD([[makeQuery(id+"F0.imprint","IMPRINT",EDGE,{"derivedFrom":subQ5}),1.0]])]});}
            var Q33;
            {var subQ1=sQuery(id+"F0.wireOp",EDGE,"E552");Q33=makeQuery(id+"F0.imprint","IMPRINT",FACE,{"disambiguationData":[TD([[makeQuery(id+"F0.imprint","IMPRINT",EDGE,{"derivedFrom":subQ1}),1.0]])]});}
            var Q34;
            {var subQ5=sQuery(id+"F0.wireOp",EDGE,"E378");Q34=makeQuery(id+"F0.imprint","IMPRINT",FACE,{"disambiguationData":[TD([[makeQuery(id+"F0.imprint","IMPRINT",EDGE,{"derivedFrom":subQ5}),1.0]])]});}
            var Q35;
            {var subQ2=sQuery(id+"F0.wireOp",EDGE,"E552");Q35=makeQuery(id+"F0.imprint","IMPRINT",FACE,{"disambiguationData":[TD([[makeQuery(id+"F0.imprint","IMPRINT",EDGE,{"derivedFrom":subQ2}),-1.0]])]});}
            var Q36;
            {var subQ4=sQuery(id+"F0.wireOp",EDGE,"E36");Q36=makeQuery(id+"F0.imprint","IMPRINT",FACE,{"disambiguationData":[TD([[makeQuery(id+"F0.imprint","IMPRINT",EDGE,{"derivedFrom":subQ4}),-1.0]])]});}
            var Q37;
            Q37=makeQuery(id+"F0.imprint","IMPRINT",FACE,{"disambiguationData":[TD([[makeQuery(id+"F0.imprint","IMPRINT",EDGE,{"derivedFrom":sQuery(id+"F0.wireOp",EDGE,"E0")}),-1.0]])]});
            var Q38;
            {var subQ0=sQuery(id+"F0.wireOp",EDGE,"E19");Q38=makeQuery(id+"F0.imprint","IMPRINT",FACE,{"disambiguationData":[TD([[makeQuery(id+"F0.imprint","IMPRINT",EDGE,{"derivedFrom":subQ0}),-1.0]])]});}
            var Q39;
            {var subQ4=sQuery(id+"F0.wireOp",EDGE,"E3");Q39=makeQuery(id+"F0.imprint","IMPRINT",FACE,{"disambiguationData":[TD([[makeQuery(id+"F0.imprint","IMPRINT",EDGE,{"derivedFrom":subQ4}),-1.0]])]});}
            var Q40;
            {var subQ4=sQuery(id+"F0.wireOp",EDGE,"E655");Q40=makeQuery(id+"F0.imprint","IMPRINT",FACE,{"disambiguationData":[TD([[makeQuery(id+"F0.imprint","IMPRINT",EDGE,{"derivedFrom":subQ4}),1.0]])]});}
            var Q41;
            {var subQ0=sQuery(id+"F0.wireOp",EDGE,"E476");var subQ1=sQuery(id+"F0.wireOp",EDGE,"E475");var subQ2=makeQuery(id+"F0.imprint","INTERSECT",VERTEX,{"derivedFrom":[subQ1,subQ0]});Q41=makeQuery(id+"F0.imprint","IMPRINT",FACE,{"disambiguationData":[TD([[makeQuery(id+"F0.imprint","IMPRINT",EDGE,{"disambiguationData":[TD([[subQ2,1.0]])],"derivedFrom":subQ1}),1.0]])]});}
            extrude(context, id + "F1", {"entities" : qUnion([Q0, Q1, Q2, Q3, Q4, Q5, Q6, Q7, Q8, Q9, Q10, Q11, Q12, Q13, Q14, Q15, Q16, Q17, Q18, Q19, Q20, Q21, Q22, Q23, Q24, Q25, Q26, Q27, Q28, Q29, Q30, Q31, Q32, Q33, Q34, Q35, Q36, Q37, Q38, Q39, Q40, Q41]), "endBound" : BoundingType.SYMMETRIC, "depth" : 8 * mm});
        }
        {
            var Q0;
            {var subQ158=sQuery(id+"F0.wireOp",EDGE,"E3");Q0=makeQuery(id+"F0.imprint","IMPRINT",FACE,{"disambiguationData":[TD([[makeQuery(id+"F0.imprint","IMPRINT",EDGE,{"derivedFrom":subQ158}),1.0]])]});}
            extrude(context, id + "F2", {"entities" : qUnion([Q0]), "endBound" : BoundingType.SYMMETRIC, "depth" : 4.5 * mm});
        }
        {
            var Q0;
            Q0=makeQuery(id+"F0.imprint","IMPRINT",FACE,{"disambiguationData":[TD([[makeQuery(id+"F0.imprint","IMPRINT",EDGE,{"derivedFrom":sQuery(id+"F0.wireOp",EDGE,"E141")}),-1.0]])]});
            extrude(context, id + "F3", {"entities" : qUnion([Q0]), "operationType" : NewBodyOperationType.ADD, "endBound" : BoundingType.SYMMETRIC, "depth" : 3.5 * mm});
        }
    });
